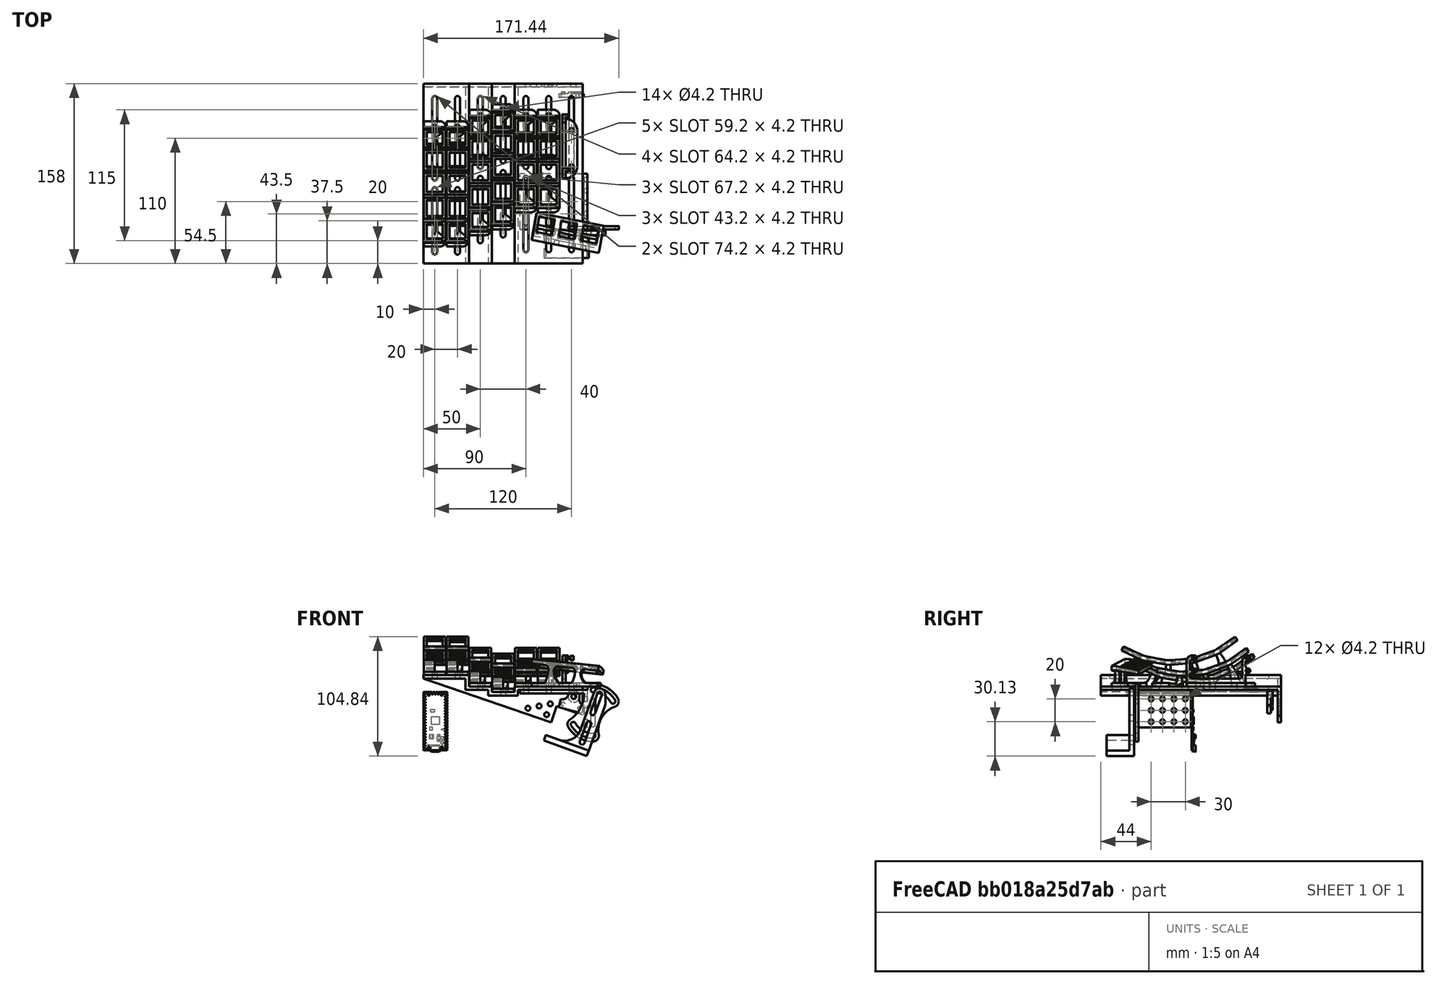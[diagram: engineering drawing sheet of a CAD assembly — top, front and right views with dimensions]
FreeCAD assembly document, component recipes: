
FREECAD ASSEMBLY — COMPONENT RECIPES ("Dactyl Chimera V3")

This assembly document has 15 components, labeled P0..P14 below (a component is one placed body or linked part). 14 of them carry a construction recipe — the FreeCAD feature program that regenerates the part from scratch, quoted from this document or its linked companion documents; the rest are supplied as boundary geometry only. No exploded tour is included for this assembly.
NOTE — document 2 of 4 of this assembly tour. The two overview renders and the header above are repeated from document 1; the component sections below continue where the previous document stopped.
COMPONENT P2 — recipe-attached ("RingArch", modeled in this document).
Construction recipe (the document's own serialized feature program — sketch geometry with constraints, then the solid features built on it; lengths are millimeters unless a unit is written):

FEATURE [Sketcher::SketchObject] Sketch012
  FullyConstrained = true
  MapMode = 5
  Placement = pos=(0,0,0) rot=(0.57735,0.57735,0.57735;2.0944rad)
  Support = -> [YZ_Plane002]
  expr: Constraints[147] = <<Spreadsheet>>.ModRowKey
  expr: Constraints[148] = <<Spreadsheet>>.ZRowKey
  expr: Constraints[149] = <<Spreadsheet>>.ARowKey
  expr: Constraints[150] = <<Spreadsheet>>.QRowKey
  expr: Constraints[151] = <<Spreadsheet>>.TopRowKey
  expr: Constraints[161] = <<Spreadsheet>>.Wiring
  sketch-geometry (61):
    g0: LineSegment StartX=-50.2141 StartY=25.1636 StartZ=0 EndX=-41.6042 EndY=21.1487 EndZ=0
    g1: LineSegment StartX=-41.6042 StartY=21.1487 StartZ=0 EndX=-32.9942 EndY=17.1338 EndZ=0
    g2: LineSegment StartX=-32.9942 StartY=17.1338 StartZ=0 EndX=-30.6407 EndY=16.3917 EndZ=0
    g3: LineSegment StartX=-30.6407 StartY=16.3917 StartZ=0 EndX=-21.285 EndY=14.7421 EndZ=0
    g4: LineSegment StartX=-21.285 StartY=14.7421 StartZ=0 EndX=-11.9293 EndY=13.0924 EndZ=0
    g5: LineSegment StartX=-11.9293 StartY=13.0924 StartZ=0 EndX=-9.46385 EndY=12.9848 EndZ=0
    g6: LineSegment StartX=-9.46385 StartY=12.9848 StartZ=0 EndX=0 EndY=13.8128 EndZ=0
    g7: LineSegment StartX=0 StartY=13.8128 StartZ=0 EndX=9.46385 EndY=14.6407 EndZ=0
    g8: LineSegment StartX=9.46385 StartY=14.6407 StartZ=0 EndX=11.8732 EndY=15.1749 EndZ=0
    g9: LineSegment StartX=11.8732 StartY=15.1749 StartZ=0 EndX=20.8002 EndY=18.4241 EndZ=0
    g10: LineSegment StartX=20.8002 StartY=18.4241 StartZ=0 EndX=29.7273 EndY=21.6733 EndZ=0
    g11: LineSegment StartX=29.7273 StartY=21.6733 StartZ=0 EndX=31.9163 EndY=22.8128 EndZ=0
    g12: LineSegment StartX=31.9163 StartY=22.8128 StartZ=0 EndX=39.6982 EndY=28.2617 EndZ=0
    g13: LineSegment StartX=39.6982 StartY=28.2617 StartZ=0 EndX=47.4802 EndY=33.7107 EndZ=0
    g14: LineSegment StartX=47.4802 StartY=33.7107 StartZ=0 EndX=49.7745 EndY=30.4341 EndZ=0
    g15: LineSegment StartX=49.7745 StartY=30.4341 StartZ=0 EndX=34.2106 EndY=19.5362 EndZ=0
    g16: LineSegment StartX=34.2106 StartY=19.5362 StartZ=0 EndX=31.0954 EndY=17.9145 EndZ=0
    g17: LineSegment StartX=31.0954 StartY=17.9145 StartZ=0 EndX=13.2412 EndY=11.4161 EndZ=0
    g18: LineSegment StartX=13.2412 StartY=11.4161 StartZ=0 EndX=9.81247 EndY=10.656 EndZ=0
    g19: LineSegment StartX=9.81247 StartY=10.656 StartZ=0 EndX=-9.11523 EndY=9 EndZ=0
    g20: LineSegment StartX=-9.11523 StartY=9 StartZ=0 EndX=-12.6239 EndY=9.15319 EndZ=0
    g21: LineSegment StartX=-12.6239 StartY=9.15319 StartZ=0 EndX=-31.3353 EndY=12.4525 EndZ=0
    g22: LineSegment StartX=-31.3353 StartY=12.4525 StartZ=0 EndX=-34.6847 EndY=13.5086 EndZ=0
    g23: LineSegment StartX=-34.6847 StartY=13.5086 StartZ=0 EndX=-51.9046 EndY=21.5383 EndZ=0
    g24: LineSegment StartX=-51.9046 StartY=21.5383 StartZ=0 EndX=-50.2141 EndY=25.1636 EndZ=0
    g25: LineSegment StartX=-34.6847 StartY=13.5086 StartZ=0 EndX=-32.9942 EndY=17.1338 EndZ=0
    g26: LineSegment StartX=-30.6407 StartY=16.3917 StartZ=0 EndX=-31.3353 EndY=12.4525 EndZ=0
    g27: LineSegment StartX=-11.9293 StartY=13.0924 StartZ=0 EndX=-12.6239 EndY=9.15319 EndZ=0
    g28: LineSegment StartX=-9.11523 StartY=9 StartZ=0 EndX=-9.46385 EndY=12.9848 EndZ=0
    g29: LineSegment StartX=9.46385 StartY=14.6407 StartZ=0 EndX=9.81247 EndY=10.656 EndZ=0
    g30: LineSegment StartX=13.2412 StartY=11.4161 StartZ=0 EndX=11.8732 EndY=15.1749 EndZ=0
    g31: LineSegment StartX=29.7273 StartY=21.6733 StartZ=0 EndX=31.0954 EndY=17.9145 EndZ=0
    g32: LineSegment StartX=34.2106 StartY=19.5362 StartZ=0 EndX=31.9163 EndY=22.8128 EndZ=0
    g33: LineSegment StartX=-41.6042 StartY=21.1487 StartZ=0 EndX=-39.4911 EndY=25.6802 EndZ=0
    g34: LineSegment StartX=-39.4911 StartY=25.6802 StartZ=0 EndX=-36.7722 EndY=24.4124 EndZ=0
    g35: LineSegment StartX=-36.7722 StartY=24.4124 StartZ=0 EndX=-32.546 EndY=33.4755 EndZ=0
    g36: LineSegment StartX=-21.6347 StartY=30.0351 StartZ=0 EndX=-23.3712 EndY=20.1871 EndZ=0
    g37: LineSegment StartX=-23.3712 StartY=20.1871 StartZ=0 EndX=-20.4167 EndY=19.6661 EndZ=0
    g38: LineSegment StartX=-20.4167 StartY=19.6661 StartZ=0 EndX=-17.4623 EndY=19.1452 EndZ=0
    g39: LineSegment StartX=-17.4623 StartY=19.1452 StartZ=0 EndX=-15.7258 EndY=28.9933 EndZ=0
    g40: LineSegment StartX=-4.29592 StartY=28.4942 StartZ=0 EndX=-3.42436 EndY=18.5323 EndZ=0
    g41: LineSegment StartX=-3.42436 StartY=18.5323 StartZ=0 EndX=-0.435779 EndY=18.7937 EndZ=0
    g42: LineSegment StartX=-0.435779 StartY=18.7937 StartZ=0 EndX=2.55281 EndY=19.0552 EndZ=0
    g43: LineSegment StartX=2.55281 StartY=19.0552 StartZ=0 EndX=1.68125 EndY=29.0171 EndZ=0
    g44: LineSegment StartX=12.8509 StartY=31.4934 StartZ=0 EndX=16.2711 EndY=22.0965 EndZ=0
    g45: LineSegment StartX=16.2711 StartY=22.0965 StartZ=0 EndX=19.0901 EndY=23.1225 EndZ=0
    g46: LineSegment StartX=19.0901 StartY=23.1225 StartZ=0 EndX=21.9092 EndY=24.1486 EndZ=0
    g47: LineSegment StartX=21.9092 StartY=24.1486 StartZ=0 EndX=18.489 EndY=33.5455 EndZ=0
    g48: LineSegment StartX=28.6371 StartY=38.8283 StartZ=0 EndX=34.3729 EndY=30.6368 EndZ=0
    g49: LineSegment StartX=34.3729 StartY=30.6368 StartZ=0 EndX=36.8304 EndY=32.3575 EndZ=0
    g50: ArcOfCircle CenterX=3.49974 CenterY=74.7282 CenterZ=0 NormalX=0 NormalY=0 NormalZ=1 AngleXU=0 Radius=43.8257 StartAngle=5.06145 EndAngle=5.32325
    g51: ArcOfCircle CenterX=-2.13841 CenterY=72.6761 CenterZ=0 NormalX=0 NormalY=0 NormalZ=1 AngleXU=0 Radius=43.8257 StartAngle=4.79966 EndAngle=5.06145
    g52: ArcOfCircle CenterX=-8.11558 CenterY=72.1532 CenterZ=0 NormalX=0 NormalY=0 NormalZ=1 AngleXU=0 Radius=43.8257 StartAngle=4.53786 EndAngle=4.79966
    g53: ArcOfCircle CenterX=-14.0244 CenterY=73.195 CenterZ=0 NormalX=0 NormalY=0 NormalZ=1 AngleXU=0 Radius=43.8257 StartAngle=4.27606 EndAngle=4.53786
    g54: LineSegment StartX=-20.4167 StartY=19.6661 StartZ=0 EndX=-21.285 EndY=14.7421 EndZ=0
    g55: LineSegment StartX=0 StartY=13.8128 StartZ=0 EndX=-0.435779 EndY=18.7937 EndZ=0
    g56: LineSegment StartX=19.0901 StartY=23.1225 StartZ=0 EndX=20.8002 EndY=18.4241 EndZ=0
    g57: LineSegment StartX=36.8304 StartY=32.3575 StartZ=0 EndX=39.6982 EndY=28.2617 EndZ=0
    g58: LineSegment StartX=-50 StartY=9 StartZ=0 EndX=-50 EndY=3 EndZ=0
    g59: LineSegment StartX=-50 StartY=9 StartZ=0 EndX=50 EndY=9 EndZ=0
    g60: LineSegment StartX=-70 StartY=9 StartZ=0 EndX=-50 EndY=9 EndZ=0
  constraints (176):
    c: Coincident(g0,g1)
    c: Coincident(g1,g2)
    c: Coincident(g2,g3)
    c: Coincident(g3,g4)
    c: Coincident(g4,g5)
    c: Coincident(g5,g6)
    c: Coincident(g6,g7)
    c: Coincident(g7,g8)
    c: Coincident(g8,g9)
    c: Coincident(g9,g10)
    c: Coincident(g10,g11)
    c: Coincident(g11,g12)
    c: Coincident(g12,g13)
    c: Coincident(g13,g14)
    c: Coincident(g14,g15)
    c: Coincident(g15,g16)
    c: Coincident(g16,g17)
    c: Coincident(g17,g18)
    c: Coincident(g18,g19)
    c: Coincident(g19,g20)
    c: Coincident(g20,g21)
    c: Coincident(g21,g22)
    c: Coincident(g22,g23)
    c: Coincident(g23,g24)
    c: Coincident(g24,g0)
    c: Coincident(g25,g22)
    c: Coincident(g25,g1)
    c: Coincident(g26,g2)
    c: Coincident(g26,g21)
    c: Coincident(g27,g4)
    c: Coincident(g27,g20)
    c: Coincident(g28,g19)
    c: Coincident(g28,g5)
    c: Coincident(g29,g7)
    c: Coincident(g29,g18)
    c: Coincident(g30,g17)
    c: Coincident(g30,g8)
    c: Coincident(g31,g10)
    c: Coincident(g31,g16)
    c: Coincident(g32,g15)
    c: Coincident(g32,g11)
    c: Equal(g32,g31)
    c: Equal(g30,g29)
    c: Equal(g28,g27)
    c: Equal(g26,g25)
    c: Perpendicular(g24,g23)
    c: Perpendicular(g23,g25)
    c: Perpendicular(g21,g26)
    c: Perpendicular(g27,g21)
    c: Perpendicular(g19,g28)
    c: Perpendicular(g29,g19)
    c: Perpendicular(g17,g30)
    c: Perpendicular(g31,g17)
    c: Perpendicular(g15,g32)
    c: Perpendicular(g14,g15)
    c: Perpendicular(g24,g0)
    c: Perpendicular(g26,g3)
    c: Perpendicular(g28,g6)
    c: Perpendicular(g30,g9)
    c: Perpendicular(g32,g12)
    c: Parallel(g13,g12)
    c: Parallel(g10,g9)
    c: Parallel(g7,g6)
    c: Parallel(g4,g3)
    c: Parallel(g1,g0)
    c: Coincident(g0,g33)
    c: Coincident(g33,g34)
    c: Coincident(g34,g35)
    c: Coincident(g36,g37)
    c: Coincident(g37,g38)
    c: Coincident(g38,g39)
    c: Coincident(g40,g41)
    c: Coincident(g41,g42)
    c: Coincident(g42,g43)
    c: Coincident(g44,g45)
    c: Coincident(g45,g46)
    c: Coincident(g46,g47)
    c: Coincident(g48,g49)
    c: Coincident(g50,g47)
    c: Coincident(g50,g48)
    c: Coincident(g51,g43)
    c: Coincident(g51,g44)
    c: Coincident(g52,g39)
    c: Coincident(g52,g40)
    c: Coincident(g53,g35)
    c: Coincident(g53,g36)
    c: Coincident(g54,g37)
    c: Coincident(g54,g3)
    c: Coincident(g55,g6)
    c: Coincident(g55,g41)
    c: Coincident(g56,g45)
    c: Coincident(g56,g9)
    c: Coincident(g57,g49)
    c: Coincident(g57,g12)
    c: Equal(g34,g37)
    c: Equal(g37,g38)
    c: Equal(g38,g41)
    c: Equal(g41,g42)
    c: Equal(g42,g45)
    c: Equal(g45,g46)
    c: Equal(g46,g49)
    c: Perpendicular(g1,g33)
    c: Perpendicular(g4,g54)
    c: Perpendicular(g7,g55)
    c: Perpendicular(g10,g56)
    c: Perpendicular(g13,g57)
    c: Perpendicular(g49,g57)
    c: Perpendicular(g46,g56)
    c: Perpendicular(g56,g45)
    c: Perpendicular(g55,g42)
    c: Perpendicular(g41,g55)
    c: Perpendicular(g54,g38)
    c: Perpendicular(g37,g54)
    c: Perpendicular(g33,g34)
    c: Perpendicular(g35,g34)
    c: Perpendicular(g53,g35)
    c: Perpendicular(g53,g36)
    c: Perpendicular(g37,g36)
    c: Perpendicular(g39,g38)
    c: Perpendicular(g52,g39)
    c: Perpendicular(g52,g40)
    c: Perpendicular(g41,g40)
    c: Perpendicular(g43,g42)
    c: Perpendicular(g51,g43)
    c: Perpendicular(g51,g44)
    c: Perpendicular(g45,g44)
    c: Perpendicular(g47,g46)
    c: Perpendicular(g50,g47)
    c: Perpendicular(g50,g48)
    c: Perpendicular(g49,g48)
    c: Distance(g33,g37) = 20
    c: Distance(g41,g37) = 20
    c: Distance(g41,g45) = 20
    c: Distance(g49,g45) = 20
    c: Equal(g13,g12)
    c: Equal(g10,g9)
    c: Equal(g7,g6)
    c: Equal(g4,g3)
    c: Equal(g1,g0)
    c: Distance(g35) = 10
    c: Distance(g36) = 10
    c: Distance(g39) = 10
    c: Distance(g40) = 10
    c: Distance(g43) = 10
    c: Distance(g44) = 10
    c: Distance(g47) = 10
    c: Distance(g48) = 10
    c: Distance(g33) = 5
    c: Distance(g54) = 5
    c: Distance(g55) = 5
    c: Distance(g56) = 5
    c: Distance(g57) = 5
    c: Distance(g19) = 19
    c: Distance(g28) = 4
    c: Equal(g23,g21)
    c: Equal(g21,g19)
    c: Equal(g19,g17)
    c: Equal(g17,g15)
    c: Vertical(g58)
    c: Coincident(g59,g58)
    c: Horizontal(g59)
    c: DistanceY(g58,g58) = 6
    c: DistanceX(g59,g59) = 100
    c: DistanceX(g58,g-1) = 50
    c: DistanceY(g-1,g58) = 3
    c: Distance(g42) = 3
    c: Horizontal(g60)
    c: Angle(g60,g55) = 1.65806
    c: Coincident(g60,g58)
    c: DistanceX(g60,g60) = 20
    c: Angle(g56,g57) = 0.261799
    c: Angle(g55,g56) = 0.261799
    c: Angle(g54,g55) = 0.261799
    c: Angle(g33,g54) = 0.261799
    c: PointOnObject(g6,g-2)
    c: PointOnObject(g19,g59)
FEATURE [PartDesign::Pad] Pad008  label="RArch"
  Direction = (1,-2e-16,3e-16)
  Length = 19
  Length2 = 100
  Midplane = true
  Placement = pos=(0,0,0) rot=(0.57735,0.57735,0.57735;2.0944rad)
  Profile = -> Sketch012
  ReferenceAxis = -> Sketch012 [N_Axis]
  Type = 0
FEATURE [Sketcher::SketchObject] Sketch013
  ExternalGeometry = -> [Sketch012]
  FullyConstrained = true
  MapMode = 5
  Placement = pos=(0,0,0) rot=(0.57735,0.57735,0.57735;2.0944rad)
  Support = -> [YZ_Plane002]
  sketch-geometry (75):
    g0: LineSegment StartX=-49.1265 StartY=24.6564 StartZ=0 EndX=-50.817 EndY=21.0312 EndZ=0
    g1: LineSegment StartX=-49.6388 StartY=20.4818 StartZ=0 EndX=-47.9483 EndY=24.107 EndZ=0
    g2: LineSegment StartX=-35.26 StartY=18.1904 StartZ=0 EndX=-36.9505 EndY=14.5651 EndZ=0
    g3: LineSegment StartX=-35.7723 StartY=14.0157 StartZ=0 EndX=-34.0818 EndY=17.641 EndZ=0
    g4: LineSegment StartX=-41.6042 StartY=21.1487 StartZ=0 EndX=-43.2946 EndY=17.5235 EndZ=0
    g5: LineSegment StartX=-29.4589 StartY=16.1834 StartZ=0 EndX=-30.1535 EndY=12.2441 EndZ=0
    g6: LineSegment StartX=-28.8732 StartY=12.0184 StartZ=0 EndX=-28.1786 EndY=15.9576 EndZ=0
    g7: LineSegment StartX=-21.285 StartY=14.7421 StartZ=0 EndX=-21.9796 EndY=10.8028 EndZ=0
    g8: LineSegment StartX=-15.0859 StartY=9.58731 StartZ=0 EndX=-14.3913 EndY=13.5265 EndZ=0
    g9: LineSegment StartX=-13.1111 StartY=13.3008 StartZ=0 EndX=-13.8057 EndY=9.36157 EndZ=0
    g10: LineSegment StartX=-8.26842 StartY=13.0894 StartZ=0 EndX=-7.91979 EndY=9.10459 EndZ=0
    g11: LineSegment StartX=-6.62474 StartY=9.21789 StartZ=0 EndX=-6.97336 EndY=13.2027 EndZ=0
    g12: LineSegment StartX=0 StartY=13.8128 StartZ=0 EndX=0.348623 EndY=9.82798 EndZ=0
    g13: LineSegment StartX=7.32199 StartY=10.4381 StartZ=0 EndX=6.97336 EndY=14.4228 EndZ=0
    g14: LineSegment StartX=8.26842 StartY=14.5362 StartZ=0 EndX=8.61704 EndY=10.5514 EndZ=0
    g15: LineSegment StartX=14.3689 StartY=11.8265 StartZ=0 EndX=13.0008 EndY=15.5853 EndZ=0
    g16: LineSegment StartX=14.2224 StartY=16.0299 StartZ=0 EndX=15.5905 EndY=12.2711 EndZ=0
    g17: LineSegment StartX=22.1683 StartY=14.6653 StartZ=0 EndX=20.8002 EndY=18.4241 EndZ=0
    g18: LineSegment StartX=27.3781 StartY=20.8182 StartZ=0 EndX=28.7462 EndY=17.0594 EndZ=0
    g19: LineSegment StartX=29.9678 StartY=17.5041 StartZ=0 EndX=28.5997 EndY=21.2628 EndZ=0
    g20: LineSegment StartX=32.8993 StartY=23.5011 StartZ=0 EndX=35.1936 EndY=20.2244 EndZ=0
    g21: LineSegment StartX=36.2585 StartY=20.9701 StartZ=0 EndX=33.9642 EndY=24.2467 EndZ=0
    g22: LineSegment StartX=39.6982 StartY=28.2617 StartZ=0 EndX=41.9925 EndY=24.9851 EndZ=0
    g23: LineSegment StartX=47.7266 StartY=29.0002 StartZ=0 EndX=45.4323 EndY=32.2768 EndZ=0
    g24: LineSegment StartX=46.4972 StartY=33.0224 StartZ=0 EndX=48.7915 EndY=29.7458 EndZ=0
    g25: LineSegment StartX=45.4323 StartY=32.2768 StartZ=0 EndX=39.6982 EndY=28.2617 EndZ=0
    g26: LineSegment StartX=39.6982 StartY=28.2617 StartZ=0 EndX=33.9642 EndY=24.2467 EndZ=0
    g27: LineSegment StartX=33.9642 StartY=24.2467 StartZ=0 EndX=34.7672 EndY=23.0999 EndZ=0
    g28: LineSegment StartX=34.7672 StartY=23.0999 StartZ=0 EndX=33.7023 EndY=22.3542 EndZ=0
    g29: LineSegment StartX=33.7023 StartY=22.3542 StartZ=0 EndX=35.1936 EndY=20.2244 EndZ=0
    g30: LineSegment StartX=35.1936 StartY=20.2244 StartZ=0 EndX=41.9925 EndY=24.9851 EndZ=0
    g31: LineSegment StartX=41.9925 StartY=24.9851 StartZ=0 EndX=48.7915 EndY=29.7458 EndZ=0
    g32: LineSegment StartX=48.7915 StartY=29.7458 StartZ=0 EndX=47.3002 EndY=31.8756 EndZ=0
    g33: LineSegment StartX=47.3002 StartY=31.8756 StartZ=0 EndX=46.2353 EndY=31.13 EndZ=0
    g34: LineSegment StartX=46.2353 StartY=31.13 StartZ=0 EndX=45.4323 EndY=32.2768 EndZ=0
    g35: LineSegment StartX=27.3781 StartY=20.8182 StartZ=0 EndX=20.8002 EndY=18.4241 EndZ=0
    g36: LineSegment StartX=20.8002 StartY=18.4241 StartZ=0 EndX=14.2224 EndY=16.0299 EndZ=0
    g37: LineSegment StartX=14.2224 StartY=16.0299 StartZ=0 EndX=14.7012 EndY=14.7144 EndZ=0
    g38: LineSegment StartX=14.7012 StartY=14.7144 StartZ=0 EndX=13.4796 EndY=14.2697 EndZ=0
    g39: LineSegment StartX=13.4796 StartY=14.2697 StartZ=0 EndX=14.3689 EndY=11.8265 EndZ=0
    g40: LineSegment StartX=14.3689 StartY=11.8265 StartZ=0 EndX=22.1683 EndY=14.6653 EndZ=0
    g41: LineSegment StartX=22.1683 StartY=14.6653 StartZ=0 EndX=29.9678 EndY=17.5041 EndZ=0
    g42: LineSegment StartX=29.9678 StartY=17.5041 StartZ=0 EndX=29.0785 EndY=19.9473 EndZ=0
    g43: LineSegment StartX=29.0785 StartY=19.9473 StartZ=0 EndX=27.8569 EndY=19.5026 EndZ=0
    g44: LineSegment StartX=27.8569 StartY=19.5026 StartZ=0 EndX=27.3781 EndY=20.8182 EndZ=0
    g45: LineSegment StartX=-6.97336 StartY=13.2027 StartZ=0 EndX=-6.85134 EndY=11.808 EndZ=0
    g46: LineSegment StartX=-6.85134 StartY=11.808 StartZ=0 EndX=-8.14639 EndY=11.6947 EndZ=0
    g47: LineSegment StartX=-8.14639 StartY=11.6947 StartZ=0 EndX=-7.91979 EndY=9.10459 EndZ=0
    g48: LineSegment StartX=8.61704 StartY=10.5514 StartZ=0 EndX=8.39044 EndY=13.1415 EndZ=0
    g49: LineSegment StartX=8.39044 StartY=13.1415 StartZ=0 EndX=7.09538 EndY=13.0282 EndZ=0
    g50: LineSegment StartX=7.09538 StartY=13.0282 StartZ=0 EndX=6.97336 EndY=14.4228 EndZ=0
    g51: LineSegment StartX=6.97336 StartY=14.4228 StartZ=0 EndX=0 EndY=13.8128 EndZ=0
    g52: LineSegment StartX=0 StartY=13.8128 StartZ=0 EndX=-6.97336 EndY=13.2027 EndZ=0
    g53: LineSegment StartX=-7.91979 StartY=9.10459 StartZ=0 EndX=0.348623 EndY=9.82798 EndZ=0
    g54: LineSegment StartX=0.348623 StartY=9.82798 StartZ=0 EndX=8.61704 EndY=10.5514 EndZ=0
    g55: LineSegment StartX=-21.285 StartY=14.7421 StartZ=0 EndX=-28.1786 EndY=15.9576 EndZ=0
    g56: LineSegment StartX=-28.1786 StartY=15.9576 StartZ=0 EndX=-28.4218 EndY=14.5789 EndZ=0
    g57: LineSegment StartX=-28.4218 StartY=14.5789 StartZ=0 EndX=-29.702 EndY=14.8046 EndZ=0
    g58: LineSegment StartX=-29.702 StartY=14.8046 StartZ=0 EndX=-30.1535 EndY=12.2441 EndZ=0
    g59: LineSegment StartX=-30.1535 StartY=12.2441 StartZ=0 EndX=-21.9796 EndY=10.8028 EndZ=0
    g60: LineSegment StartX=-21.9796 StartY=10.8028 StartZ=0 EndX=-13.8057 EndY=9.36157 EndZ=0
    g61: LineSegment StartX=-13.8057 StartY=9.36157 StartZ=0 EndX=-13.3542 EndY=11.9221 EndZ=0
    g62: LineSegment StartX=-13.3542 StartY=11.9221 StartZ=0 EndX=-14.6345 EndY=12.1478 EndZ=0
    g63: LineSegment StartX=-14.6345 StartY=12.1478 StartZ=0 EndX=-14.3913 EndY=13.5265 EndZ=0
    g64: LineSegment StartX=-14.3913 StartY=13.5265 StartZ=0 EndX=-21.285 EndY=14.7421 EndZ=0
    g65: LineSegment StartX=-41.6042 StartY=21.1487 StartZ=0 EndX=-47.9483 EndY=24.107 EndZ=0
    g66: LineSegment StartX=-47.9483 StartY=24.107 StartZ=0 EndX=-48.54 EndY=22.8382 EndZ=0
    g67: LineSegment StartX=-48.54 StartY=22.8382 StartZ=0 EndX=-49.7182 EndY=23.3876 EndZ=0
    g68: LineSegment StartX=-49.7182 StartY=23.3876 StartZ=0 EndX=-50.817 EndY=21.0312 EndZ=0
    g69: LineSegment StartX=-50.817 StartY=21.0312 StartZ=0 EndX=-43.2946 EndY=17.5235 EndZ=0
    g70: LineSegment StartX=-43.2946 StartY=17.5235 StartZ=0 EndX=-35.7723 EndY=14.0157 EndZ=0
    g71: LineSegment StartX=-35.7723 StartY=14.0157 StartZ=0 EndX=-34.6735 EndY=16.3721 EndZ=0
    g72: LineSegment StartX=-34.6735 StartY=16.3721 StartZ=0 EndX=-35.8517 EndY=16.9215 EndZ=0
    g73: LineSegment StartX=-35.8517 StartY=16.9215 StartZ=0 EndX=-35.26 EndY=18.1904 EndZ=0
    g74: LineSegment StartX=-35.26 StartY=18.1904 StartZ=0 EndX=-41.6042 EndY=21.1487 EndZ=0
  constraints (215):
    c: PointOnObject(g0,g-16)
    c: PointOnObject(g0,g-17)
    c: PointOnObject(g1,g-17)
    c: PointOnObject(g1,g-16)
    c: PointOnObject(g2,g-15)
    c: PointOnObject(g2,g-17)
    c: PointOnObject(g3,g-17)
    c: PointOnObject(g3,g-15)
    c: Coincident(g4,g-16)
    c: PointOnObject(g4,g-17)
    c: PointOnObject(g5,g-14)
    c: PointOnObject(g5,g-12)
    c: PointOnObject(g6,g-12)
    c: PointOnObject(g6,g-14)
    c: Coincident(g7,g-14)
    c: PointOnObject(g7,g-12)
    c: PointOnObject(g8,g-12)
    c: PointOnObject(g8,g-13)
    c: PointOnObject(g9,g-13)
    c: PointOnObject(g9,g-12)
    c: PointOnObject(g10,g-10)
    c: PointOnObject(g10,g-11)
    c: PointOnObject(g11,g-11)
    c: PointOnObject(g11,g-10)
    c: Coincident(g12,g-10)
    c: PointOnObject(g12,g-11)
    c: PointOnObject(g13,g-9)
    c: PointOnObject(g14,g-9)
    c: PointOnObject(g14,g-11)
    c: PointOnObject(g15,g-6)
    c: PointOnObject(g15,g-8)
    c: PointOnObject(g16,g-8)
    c: PointOnObject(g16,g-6)
    c: PointOnObject(g17,g-6)
    c: Coincident(g17,g-8)
    c: PointOnObject(g18,g-7)
    c: PointOnObject(g18,g-6)
    c: PointOnObject(g19,g-6)
    c: PointOnObject(g19,g-7)
    c: PointOnObject(g20,g-4)
    c: PointOnObject(g20,g-5)
    c: PointOnObject(g21,g-5)
    c: PointOnObject(g21,g-4)
    c: Coincident(g22,g-4)
    c: PointOnObject(g22,g-5)
    c: PointOnObject(g23,g-5)
    c: PointOnObject(g23,g-3)
    c: PointOnObject(g24,g-3)
    c: PointOnObject(g24,g-5)
    c: Perpendicular(g-3,g24)
    c: Perpendicular(g23,g-3)
    c: Perpendicular(g22,g-5)
    c: Perpendicular(g21,g-4)
    c: Perpendicular(g20,g-4)
    c: Perpendicular(g-7,g19)
    c: Perpendicular(g-6,g17)
    c: Perpendicular(g-8,g16)
    c: Perpendicular(g15,g-8)
    c: Perpendicular(g-9,g14)
    c: Perpendicular(g13,g-9)
    c: Perpendicular(g12,g-11)
    c: Perpendicular(g-10,g11)
    c: Perpendicular(g-10,g10)
    c: Perpendicular(g-13,g9)
    c: Perpendicular(g-13,g8)
    c: Perpendicular(g-12,g7)
    c: Perpendicular(g-14,g6)
    c: Perpendicular(g-14,g5)
    c: Perpendicular(g-15,g3)
    c: Perpendicular(g2,g-15)
    c: Perpendicular(g-17,g4)
    c: Perpendicular(g-16,g1)
    c: Perpendicular(g-16,g0)
    c: Distance(g2,g1) = 14
    c: Distance(g3,g0) = 16.6
    c: Distance(g6,g8) = 14
    c: Distance(g9,g5) = 16.6
    c: Distance(g13,g11) = 14
    c: Distance(g14,g10) = 16.6
    c: Distance(g15,g19) = 16.6
    c: Distance(g16,g18) = 14
    c: Perpendicular(g-7,g18)
    c: Distance(g24,g20) = 16.6
    c: Distance(g23,g21) = 14
    c: Coincident(g23,g25)
    c: Coincident(g25,g22)
    c: Coincident(g25,g26)
    c: Coincident(g26,g21)
    c: Coincident(g26,g27)
    c: Coincident(g27,g28)
    c: Coincident(g28,g29)
    c: Coincident(g29,g20)
    c: Coincident(g29,g30)
    c: Coincident(g30,g22)
    c: Coincident(g30,g31)
    c: Coincident(g31,g24)
    c: Coincident(g31,g32)
    c: Coincident(g32,g33)
    c: Coincident(g33,g34)
    c: Coincident(g34,g25)
    c: Equal(g25,g26)
    c: Equal(g31,g30)
    c: Distance(g26,g27) = 1.4
    c: Distance(g27,g21) = 2.6
    c: Distance(g29,g28) = 2.6
    c: Distance(g28,g20) = 1.4
    c: Distance(g33,g25) = 1.4
    c: Distance(g32,g24) = 1.4
    c: Distance(g32,g31) = 2.6
    c: Distance(g33,g23) = 2.6
    c: Coincident(g18,g35)
    c: Coincident(g35,g17)
    c: Coincident(g35,g36)
    c: Coincident(g36,g16)
    c: Coincident(g36,g37)
    c: Coincident(g37,g38)
    c: Coincident(g38,g39)
    c: Coincident(g39,g15)
    c: Coincident(g39,g40)
    c: Coincident(g40,g17)
    c: Coincident(g40,g41)
    c: Coincident(g41,g19)
    c: Coincident(g41,g42)
    c: Coincident(g42,g43)
    c: Coincident(g43,g44)
    c: Coincident(g44,g35)
    c: Coincident(g45,g46)
    c: Coincident(g46,g47)
    c: Coincident(g47,g10)
    c: Coincident(g48,g49)
    c: Coincident(g49,g50)
    c: Coincident(g50,g51)
    c: Coincident(g51,g12)
    c: Coincident(g51,g52)
    c: Coincident(g52,g45)
    c: Equal(g52,g51)
    c: Coincident(g45,g11)
    c: Coincident(g50,g13)
    c: Distance(g50,g49) = 1.4
    c: Distance(g13,g49) = 2.6
    c: Distance(g14,g48) = 1.4
    c: Distance(g48,g14) = 2.6
    c: Coincident(g47,g53)
    c: Coincident(g53,g12)
    c: Coincident(g53,g54)
    c: Coincident(g54,g48)
    c: Coincident(g48,g14)
    c: Equal(g54,g53)
    c: PointOnObject(g13,g-11)
    c: Distance(g45,g45) = 1.4
    c: Distance(g45,g11) = 2.6
    c: Distance(g10,g46) = 1.4
    c: Distance(g46,g47) = 2.6
    c: Coincident(g7,g55)
    c: Coincident(g55,g56)
    c: Coincident(g56,g57)
    c: Coincident(g57,g58)
    c: Coincident(g58,g5)
    c: Coincident(g58,g59)
    c: Coincident(g59,g60)
    c: Coincident(g60,g9)
    c: Coincident(g60,g61)
    c: Coincident(g61,g62)
    c: Coincident(g62,g63)
    c: Coincident(g63,g8)
    c: Coincident(g63,g64)
    c: Coincident(g64,g55)
    c: Coincident(g55,g6)
    c: Equal(g55,g64)
    c: Coincident(g59,g7)
    c: Equal(g59,g60)
    c: Distance(g61,g60) = 2.6
    c: Distance(g62,g8) = 2.6
    c: Distance(g57,g5) = 1.4
    c: Distance(g55,g56) = 1.4
    c: Distance(g6,g56) = 2.6
    c: Distance(g57,g58) = 2.6
    c: Distance(g62,g63) = 1.4
    c: Distance(g61,g9) = 1.4
    c: Coincident(g4,g65)
    c: Coincident(g65,g1)
    c: Coincident(g65,g66)
    c: Coincident(g66,g67)
    c: Coincident(g67,g68)
    c: Coincident(g68,g0)
    c: Coincident(g68,g69)
    c: Coincident(g69,g4)
    c: Coincident(g69,g70)
    c: Coincident(g70,g3)
    c: Coincident(g70,g71)
    c: Coincident(g71,g72)
    c: Coincident(g72,g73)
    c: Coincident(g73,g2)
    c: Coincident(g73,g74)
    c: Coincident(g74,g65)
    c: Equal(g74,g65)
    c: Equal(g70,g69)
    c: Distance(g73,g72) = 1.4
    c: Distance(g71,g3) = 1.4
    c: Distance(g72,g2) = 2.6
    c: Distance(g70,g71) = 2.6
    c: Distance(g66,g65) = 1.4
    c: Distance(g0,g67) = 1.4
    c: Distance(g67,g68) = 2.6
    c: Distance(g66,g1) = 2.6
    c: Equal(g36,g35)
    c: Equal(g41,g40)
    c: Distance(g41,g42) = 2.6
    c: Distance(g42,g19) = 1.4
    c: Distance(g43,g35) = 1.4
    c: Distance(g43,g18) = 2.6
    c: Distance(g37,g36) = 1.4
    c: Distance(g38,g15) = 1.4
    c: Distance(g38,g39) = 2.6
    c: Distance(g37,g16) = 2.6
FEATURE [PartDesign::Pocket] Pocket004  label="RMX sockets"
  BaseFeature = -> Pad008
  Direction = (-1,2e-16,-3e-16)
  Length = 14
  Length2 = 100
  Midplane = true
  Placement = pos=(0,0,0) rot=(0.57735,0.57735,0.57735;2.0944rad)
  Profile = -> Sketch013
  Type = 0
FEATURE [Sketcher::SketchObject] Sketch014
  ExternalGeometry = -> [Sketch013]
  FullyConstrained = true
  MapMode = 5
  Placement = pos=(0,0,0) rot=(0.57735,0.57735,0.57735;2.0944rad)
  Support = -> [YZ_Plane002]
  sketch-geometry (55):
    g0: LineSegment StartX=27.8569 StartY=19.5026 StartZ=0 EndX=27.7885 EndY=19.6906 EndZ=0
    g1: LineSegment StartX=27.7885 StartY=19.6906 StartZ=0 EndX=14.6328 EndY=14.9023 EndZ=0
    g2: LineSegment StartX=14.6328 StartY=14.9023 StartZ=0 EndX=14.7012 EndY=14.7144 EndZ=0
    g3: LineSegment StartX=14.7012 StartY=14.7144 StartZ=0 EndX=13.4796 EndY=14.2697 EndZ=0
    g4: LineSegment StartX=13.4796 StartY=14.2697 StartZ=0 EndX=13.7532 EndY=13.518 EndZ=0
    g5: LineSegment StartX=13.7532 StartY=13.518 StartZ=0 EndX=29.3521 EndY=19.1955 EndZ=0
    g6: LineSegment StartX=29.3521 StartY=19.1955 StartZ=0 EndX=29.0785 EndY=19.9473 EndZ=0
    g7: LineSegment StartX=29.0785 StartY=19.9473 StartZ=0 EndX=27.8569 EndY=19.5026 EndZ=0
    g8: LineSegment StartX=7.07795 StartY=13.2274 StartZ=0 EndX=7.09538 EndY=13.0282 EndZ=0
    g9: LineSegment StartX=7.09538 StartY=13.0282 StartZ=0 EndX=8.39044 EndY=13.1415 EndZ=0
    g10: LineSegment StartX=8.39044 StartY=13.1415 StartZ=0 EndX=8.46016 EndY=12.3445 EndZ=0
    g11: LineSegment StartX=8.46016 StartY=12.3445 StartZ=0 EndX=-8.07667 EndY=10.8977 EndZ=0
    g12: LineSegment StartX=-8.07667 StartY=10.8977 StartZ=0 EndX=-8.14639 EndY=11.6947 EndZ=0
    g13: LineSegment StartX=-8.14639 StartY=11.6947 StartZ=0 EndX=-6.85134 EndY=11.808 EndZ=0
    g14: LineSegment StartX=-6.85134 StartY=11.808 StartZ=0 EndX=-6.86877 EndY=12.0072 EndZ=0
    g15: LineSegment StartX=-6.86877 StartY=12.0072 StartZ=0 EndX=7.07795 EndY=13.2274 EndZ=0
    g16: LineSegment StartX=0 StartY=13.8128 StartZ=0 EndX=0.104587 EndY=12.6173 EndZ=0
    g17: LineSegment StartX=0.104587 StartY=12.6173 StartZ=0 EndX=0.191743 EndY=11.6211 EndZ=0
    g18: LineSegment StartX=0.191743 StartY=11.6211 StartZ=0 EndX=0.348623 EndY=9.82798 EndZ=0
    g19: LineSegment StartX=20.8002 StartY=18.4241 StartZ=0 EndX=21.2107 EndY=17.2964 EndZ=0
    g20: LineSegment StartX=21.2107 StartY=17.2964 StartZ=0 EndX=21.5527 EndY=16.3567 EndZ=0
    g21: LineSegment StartX=21.5527 StartY=16.3567 StartZ=0 EndX=22.1683 EndY=14.6653 EndZ=0
    g22: LineSegment StartX=39.6982 StartY=28.2617 StartZ=0 EndX=40.3865 EndY=27.2788 EndZ=0
    g23: LineSegment StartX=40.3865 StartY=27.2788 StartZ=0 EndX=40.9601 EndY=26.4596 EndZ=0
    g24: LineSegment StartX=40.9601 StartY=26.4596 StartZ=0 EndX=41.9925 EndY=24.9851 EndZ=0
    g25: LineSegment StartX=34.6525 StartY=23.2637 StartZ=0 EndX=46.1206 EndY=31.2938 EndZ=0
    g26: LineSegment StartX=46.1206 StartY=31.2938 StartZ=0 EndX=46.2353 EndY=31.13 EndZ=0
    g27: LineSegment StartX=46.2353 StartY=31.13 StartZ=0 EndX=47.3002 EndY=31.8756 EndZ=0
    g28: LineSegment StartX=47.3002 StartY=31.8756 StartZ=0 EndX=47.7591 EndY=31.2203 EndZ=0
    g29: LineSegment StartX=47.7591 StartY=31.2203 StartZ=0 EndX=34.1611 EndY=21.6989 EndZ=0
    g30: LineSegment StartX=34.1611 StartY=21.6989 StartZ=0 EndX=33.7023 EndY=22.3542 EndZ=0
    g31: LineSegment StartX=33.7023 StartY=22.3542 StartZ=0 EndX=34.7672 EndY=23.0999 EndZ=0
    g32: LineSegment StartX=34.7672 StartY=23.0999 StartZ=0 EndX=34.6525 EndY=23.2637 EndZ=0
    g33: LineSegment StartX=-48.54 StartY=22.8382 StartZ=0 EndX=-49.7182 EndY=23.3876 EndZ=0
    g34: LineSegment StartX=-49.7182 StartY=23.3876 StartZ=0 EndX=-50.0563 EndY=22.6626 EndZ=0
    g35: LineSegment StartX=-50.0563 StartY=22.6626 StartZ=0 EndX=-35.0116 EndY=15.6471 EndZ=0
    g36: LineSegment StartX=-35.0116 StartY=15.6471 StartZ=0 EndX=-34.6735 EndY=16.3721 EndZ=0
    g37: LineSegment StartX=-34.6735 StartY=16.3721 StartZ=0 EndX=-35.8517 EndY=16.9215 EndZ=0
    g38: LineSegment StartX=-35.8517 StartY=16.9215 StartZ=0 EndX=-35.7672 EndY=17.1028 EndZ=0
    g39: LineSegment StartX=-35.7672 StartY=17.1028 StartZ=0 EndX=-48.4555 EndY=23.0195 EndZ=0
    g40: LineSegment StartX=-48.4555 StartY=23.0195 StartZ=0 EndX=-48.54 EndY=22.8382 EndZ=0
    g41: LineSegment StartX=-41.6042 StartY=21.1487 StartZ=0 EndX=-42.1113 EndY=20.0611 EndZ=0
    g42: LineSegment StartX=-42.1113 StartY=20.0611 StartZ=0 EndX=-42.5339 EndY=19.1548 EndZ=0
    g43: LineSegment StartX=-42.5339 StartY=19.1548 StartZ=0 EndX=-43.2946 EndY=17.5235 EndZ=0
    g44: LineSegment StartX=-28.387 StartY=14.7758 StartZ=0 EndX=-28.4218 EndY=14.5789 EndZ=0
    g45: LineSegment StartX=-28.4218 StartY=14.5789 StartZ=0 EndX=-29.702 EndY=14.8046 EndZ=0
    g46: LineSegment StartX=-29.702 StartY=14.8046 StartZ=0 EndX=-29.8409 EndY=14.0168 EndZ=0
    g47: LineSegment StartX=-29.8409 StartY=14.0168 StartZ=0 EndX=-13.4931 EndY=11.1342 EndZ=0
    g48: LineSegment StartX=-13.4931 StartY=11.1342 StartZ=0 EndX=-13.3542 EndY=11.9221 EndZ=0
    g49: LineSegment StartX=-13.3542 StartY=11.9221 StartZ=0 EndX=-14.6345 EndY=12.1478 EndZ=0
    g50: LineSegment StartX=-14.6345 StartY=12.1478 StartZ=0 EndX=-14.5997 EndY=12.3448 EndZ=0
    g51: LineSegment StartX=-14.5997 StartY=12.3448 StartZ=0 EndX=-28.387 EndY=14.7758 EndZ=0
    g52: LineSegment StartX=-21.285 StartY=14.7421 StartZ=0 EndX=-21.4934 EndY=13.5603 EndZ=0
    g53: LineSegment StartX=-21.4934 StartY=13.5603 StartZ=0 EndX=-21.667 EndY=12.5755 EndZ=0
    g54: LineSegment StartX=-21.667 StartY=12.5755 StartZ=0 EndX=-21.9796 EndY=10.8028 EndZ=0
  constraints (140):
    c: Coincident(g-3,g0)
    c: Coincident(g0,g1)
    c: Coincident(g1,g2)
    c: Coincident(g2,g3)
    c: Coincident(g3,g4)
    c: Coincident(g4,g5)
    c: Coincident(g5,g6)
    c: Coincident(g6,g-4)
    c: Coincident(g6,g7)
    c: Coincident(g7,g0)
    c: Coincident(g3,g-6)
    c: Coincident(g2,g-5)
    c: Coincident(g8,g-7)
    c: Coincident(g8,g9)
    c: Coincident(g9,g-8)
    c: Coincident(g9,g10)
    c: Coincident(g10,g11)
    c: Coincident(g11,g12)
    c: Coincident(g12,g-9)
    c: Coincident(g12,g13)
    c: Coincident(g13,g-10)
    c: Coincident(g13,g14)
    c: Coincident(g14,g15)
    c: Coincident(g15,g8)
    c: PointOnObject(g10,g-8)
    c: PointOnObject(g1,g-5)
    c: PointOnObject(g0,g-3)
    c: PointOnObject(g5,g-4)
    c: PointOnObject(g4,g-6)
    c: PointOnObject(g8,g-7)
    c: PointOnObject(g11,g-9)
    c: PointOnObject(g14,g-10)
    c: Coincident(g16,g-11)
    c: PointOnObject(g16,g15)
    c: Coincident(g17,g16)
    c: PointOnObject(g17,g11)
    c: Coincident(g18,g-12)
    c: Angle(g16,g17) = 3.14159
    c: Angle(g17,g18) = 3.14159
    c: Coincident(g17,g18)
    c: Perpendicular(g16,g15)
    c: Perpendicular(g18,g11)
    c: Distance(g16) = 1.2
    c: Distance(g18) = 1.8
    c: Coincident(g19,g-13)
    c: PointOnObject(g19,g1)
    c: Coincident(g19,g20)
    c: PointOnObject(g20,g5)
    c: Coincident(g20,g21)
    c: Coincident(g21,g-14)
    c: Angle(g21,g20) = 3.14159
    c: Angle(g19,g20) = 3.14159
    c: Perpendicular(g21,g5)
    c: Perpendicular(g1,g19)
    c: Distance(g19) = 1.2
    c: Distance(g21) = 1.8
    c: Coincident(g22,g-16)
    c: Coincident(g22,g23)
    c: Coincident(g23,g24)
    c: Coincident(g24,g-15)
    c: PointOnObject(g25,g-17)
    c: PointOnObject(g25,g-20)
    c: Coincident(g25,g26)
    c: Coincident(g26,g-20)
    c: Coincident(g26,g27)
    c: Coincident(g27,g-19)
    c: Coincident(g27,g28)
    c: PointOnObject(g28,g-19)
    c: Coincident(g28,g29)
    c: PointOnObject(g29,g-18)
    c: Coincident(g29,g30)
    c: Coincident(g30,g-18)
    c: Coincident(g30,g31)
    c: Coincident(g31,g-17)
    c: Coincident(g31,g32)
    c: Coincident(g32,g25)
    c: PointOnObject(g22,g25)
    c: PointOnObject(g23,g29)
    c: Angle(g23,g24) = 3.14159
    c: Angle(g23,g22) = 3.14159
    c: Distance(g22) = 1.2
    c: Distance(g24) = 1.8
    c: Perpendicular(g23,g29)
    c: Perpendicular(g23,g25)
    c: Coincident(g-29,g33)
    c: Coincident(g33,g-30)
    c: Coincident(g33,g34)
    c: PointOnObject(g34,g-30)
    c: Coincident(g34,g35)
    c: PointOnObject(g35,g-27)
    c: Coincident(g35,g36)
    c: Coincident(g36,g-27)
    c: Coincident(g36,g37)
    c: Coincident(g37,g-28)
    c: Coincident(g37,g38)
    c: PointOnObject(g38,g-28)
    c: Coincident(g38,g39)
    c: PointOnObject(g39,g-29)
    c: Coincident(g39,g40)
    c: Coincident(g40,g33)
    c: Coincident(g-32,g41)
    c: PointOnObject(g41,g39)
    c: Coincident(g41,g42)
    c: PointOnObject(g42,g35)
    c: Coincident(g42,g43)
    c: Coincident(g-31,g43)
    c: Angle(g42,g41) = 3.14159
    c: Angle(g43,g42) = 3.14159
    c: Distance(g41) = 1.2
    c: Distance(g42) = 1
    c: Perpendicular(g42,g39)
    c: Perpendicular(g43,g35)
    c: PointOnObject(g44,g-24)
    c: Coincident(g44,g-24)
    c: Coincident(g44,g45)
    c: Coincident(g45,g-25)
    c: Coincident(g45,g46)
    c: PointOnObject(g46,g-25)
    c: Coincident(g46,g47)
    c: PointOnObject(g47,g-22)
    c: Coincident(g47,g48)
    c: Coincident(g48,g49)
    c: Coincident(g49,g-23)
    c: Coincident(g49,g50)
    c: Coincident(g50,g51)
    c: Coincident(g51,g44)
    c: Coincident(g-22,g48)
    c: PointOnObject(g50,g-23)
    c: Coincident(g-26,g52)
    c: PointOnObject(g52,g51)
    c: Coincident(g52,g53)
    c: PointOnObject(g53,g47)
    c: Coincident(g53,g54)
    c: Coincident(g54,g-21)
    c: Angle(g52,g53) = 3.14159
    c: Angle(g54,g53) = 3.14159
    c: Distance(g52) = 1.2
    c: Distance(g53) = 1
    c: Perpendicular(g51,g52)
    c: Perpendicular(g47,g54)
FEATURE [PartDesign::Pocket] Pocket005  label="RChoc sockets"
  BaseFeature = -> Pocket004
  Direction = (-1,2e-16,-3e-16)
  Length = 14.6
  Length2 = 100
  Midplane = true
  Placement = pos=(0,0,0) rot=(0.57735,0.57735,0.57735;2.0944rad)
  Profile = -> Sketch014
  Type = 0
FEATURE [Sketcher::SketchObject] Sketch017
  ExternalGeometry = -> [Sketch012]
  FullyConstrained = true
  MapMode = 5
  Placement = pos=(0,0,0) rot=(0.57735,0.57735,0.57735;2.0944rad)
  Support = -> [YZ_Plane002]
  expr: Constraints[39] = <<Spreadsheet>>.Wiring
  sketch-geometry (16):
    g0: LineSegment StartX=-13.6658 StartY=3.24435 StartZ=0 EndX=-12.6239 EndY=9.15319 EndZ=0
    g1: LineSegment StartX=-12.6239 StartY=9.15319 StartZ=0 EndX=-11.9293 EndY=13.0924 EndZ=0
    g2: LineSegment StartX=-11.9293 StartY=13.0924 StartZ=0 EndX=-9.46385 EndY=12.9848 EndZ=0
    g3: LineSegment StartX=-9.46385 StartY=12.9848 StartZ=0 EndX=-9.11523 EndY=9 EndZ=0
    g4: LineSegment StartX=-9.11523 StartY=9 StartZ=0 EndX=-8.59229 EndY=3.02283 EndZ=0
    g5: LineSegment StartX=-8.59229 StartY=3.02283 StartZ=0 EndX=-8.59229 EndY=0 EndZ=0
    g6: LineSegment StartX=-8.59229 StartY=0 StartZ=0 EndX=-13.6658 EndY=0 EndZ=0
    g7: LineSegment StartX=-13.6658 StartY=0 StartZ=0 EndX=-13.6658 EndY=3.24435 EndZ=0
    g8: LineSegment StartX=15.2934 StartY=0 StartZ=0 EndX=10.3354 EndY=0 EndZ=0
    g9: LineSegment StartX=10.3354 StartY=0 StartZ=0 EndX=10.3354 EndY=4.67879 EndZ=0
    g10: LineSegment StartX=10.3354 StartY=4.67879 StartZ=0 EndX=9.81247 EndY=10.656 EndZ=0
    g11: LineSegment StartX=9.81247 StartY=10.656 StartZ=0 EndX=9.46385 EndY=14.6407 EndZ=0
    g12: LineSegment StartX=9.46385 StartY=14.6407 StartZ=0 EndX=11.8732 EndY=15.1749 EndZ=0
    g13: LineSegment StartX=11.8732 StartY=15.1749 StartZ=0 EndX=13.2412 EndY=11.4161 EndZ=0
    g14: LineSegment StartX=13.2412 StartY=11.4161 StartZ=0 EndX=15.2934 EndY=5.77794 EndZ=0
    g15: LineSegment StartX=15.2934 StartY=5.77794 StartZ=0 EndX=15.2934 EndY=0 EndZ=0
  constraints (40):
    c: Coincident(g0,g-4)
    c: Coincident(g0,g1)
    c: Coincident(g1,g-3)
    c: Coincident(g1,g2)
    c: Coincident(g2,g-3)
    c: Coincident(g2,g3)
    c: Coincident(g3,g-4)
    c: Coincident(g3,g4)
    c: Coincident(g4,g5)
    c: PointOnObject(g5,g-1)
    c: Vertical(g5)
    c: Coincident(g5,g6)
    c: PointOnObject(g6,g-1)
    c: Coincident(g6,g7)
    c: Coincident(g7,g0)
    c: Vertical(g7)
    c: Angle(g4,g3) = 3.14159
    c: Angle(g1,g0) = 3.14159
    c: PointOnObject(g8,g-1)
    c: PointOnObject(g8,g-1)
    c: Coincident(g8,g9)
    c: Vertical(g9)
    c: Coincident(g9,g10)
    c: Coincident(g10,g-6)
    c: Coincident(g10,g11)
    c: Coincident(g11,g-5)
    c: Coincident(g11,g12)
    c: Coincident(g12,g-5)
    c: Coincident(g12,g13)
    c: Coincident(g13,g-6)
    c: Coincident(g13,g14)
    c: Coincident(g14,g15)
    c: Coincident(g15,g8)
    c: Vertical(g15)
    c: Equal(g0,g4)
    c: Equal(g4,g10)
    c: Equal(g10,g14)
    c: Angle(g11,g10) = 3.14159
    c: Angle(g13,g14) = 3.14159
    c: Distance(g0) = 6
FEATURE [PartDesign::Pad] Pad009  label="RInner legs"
  BaseFeature = -> Pocket005
  Direction = (1,-2e-16,3e-16)
  Length = 4.1
  Length2 = 9.5
  Placement = pos=(0,0,0) rot=(0.57735,0.57735,0.57735;2.0944rad)
  Profile = -> Sketch017
  Type = 4
  expr: Length = <<Spreadsheet>>.ScrewD / 2 + 2mm
FEATURE [Sketcher::SketchObject] Sketch018
  ExternalGeometry = -> [Sketch012]
  FullyConstrained = true
  MapMode = 5
  Placement = pos=(0,0,0) rot=(0.57735,0.57735,0.57735;2.0944rad)
  Support = -> [YZ_Plane002]
  expr: Constraints[53] = <<Spreadsheet>>.ArchLength
  expr: Constraints[54] = <<Spreadsheet>>.ArchLength - 5mm
  expr: Constraints[56] = <<Spreadsheet>>.ArchLength - 10mm
  expr: Constraints[57] = <<Spreadsheet>>.ArchLength
  expr: Constraints[58] = <<Spreadsheet>>.ArchLength - 5mm
  expr: Constraints[73] = <<Spreadsheet>>.ArchLength - 10mm
  sketch-geometry (36):
    g0: LineSegment StartX=-37.2204 StartY=8.07075 StartZ=0 EndX=-34.6847 EndY=13.5086 EndZ=0
    g1: LineSegment StartX=-34.6847 StartY=13.5086 StartZ=0 EndX=-32.9942 EndY=17.1338 EndZ=0
    g2: LineSegment StartX=-32.9942 StartY=17.1338 StartZ=0 EndX=-30.6407 EndY=16.3917 EndZ=0
    g3: LineSegment StartX=-30.6407 StartY=16.3917 StartZ=0 EndX=-31.3353 EndY=12.4525 EndZ=0
    g4: LineSegment StartX=-31.3353 StartY=12.4525 StartZ=0 EndX=-32.3771 EndY=6.54366 EndZ=0
    g5: LineSegment StartX=33.1475 StartY=12.2763 StartZ=0 EndX=31.0954 EndY=17.9145 EndZ=0
    g6: LineSegment StartX=31.0954 StartY=17.9145 StartZ=0 EndX=29.7273 EndY=21.6733 EndZ=0
    g7: LineSegment StartX=29.7273 StartY=21.6733 StartZ=0 EndX=31.9163 EndY=22.8128 EndZ=0
    g8: LineSegment StartX=31.9163 StartY=22.8128 StartZ=0 EndX=34.2106 EndY=19.5362 EndZ=0
    g9: LineSegment StartX=34.2106 StartY=19.5362 StartZ=0 EndX=37.6521 EndY=14.6212 EndZ=0
    g10: LineSegment StartX=-37.2204 StartY=8.07075 StartZ=0 EndX=-39.0097 EndY=4.23371 EndZ=0
    g11: LineSegment StartX=-39.0097 StartY=4.23371 StartZ=0 EndX=-39.0097 EndY=0 EndZ=0
    g12: LineSegment StartX=37.6521 StartY=14.6212 StartZ=0 EndX=42.2621 EndY=8.03739 EndZ=0
    g13: LineSegment StartX=42.2621 StartY=8.03739 StartZ=0 EndX=42.2621 EndY=0 EndZ=0
    g14: LineSegment StartX=-32.3771 StartY=6.54366 StartZ=0 EndX=-35 EndY=0 EndZ=0
    g15: LineSegment StartX=-35 StartY=0 StartZ=0 EndX=-45 EndY=0 EndZ=0
    g16: LineSegment StartX=-45 StartY=0 StartZ=0 EndX=-45 EndY=3 EndZ=0
    g17: LineSegment StartX=-45 StartY=3 StartZ=0 EndX=-40 EndY=3 EndZ=0
    g18: LineSegment StartX=40 StartY=3 StartZ=0 EndX=45 EndY=3 EndZ=0
    g19: LineSegment StartX=45 StartY=3 StartZ=0 EndX=45 EndY=0 EndZ=0
    g20: LineSegment StartX=45 StartY=0 StartZ=0 EndX=35 EndY=0 EndZ=0
    g21: LineSegment StartX=35 StartY=0 StartZ=0 EndX=33.1475 EndY=12.2763 EndZ=0
    g22-g25: Circle x4 (B-spline internal-alignment scaffolding for g26; pole/knot coordinates omitted)
    g26: BSplineCurve PolesCount=4 KnotsCount=2 Degree=3 IsPeriodic=0
    g27: GeomPoint X=-37.2204 Y=8.07075 Z=0
    g28: GeomPoint X=-45 Y=3 Z=0
    g29-g32: Circle x4 (B-spline internal-alignment scaffolding for g33; pole/knot coordinates omitted)
    g33: BSplineCurve PolesCount=4 KnotsCount=2 Degree=3 IsPeriodic=0
    g34: GeomPoint X=37.6521 Y=14.6212 Z=0
    g35: GeomPoint X=45 Y=3 Z=0
  constraints (82):
    c: Coincident(g0,g-6)
    c: Coincident(g0,g1)
    c: Coincident(g1,g-5)
    c: Coincident(g1,g2)
    c: Coincident(g2,g-5)
    c: Coincident(g2,g3)
    c: Coincident(g3,g-6)
    c: Coincident(g3,g4)
    c: Coincident(g5,g-3)
    c: Coincident(g5,g6)
    c: Coincident(g6,g-4)
    c: Coincident(g6,g7)
    c: Coincident(g7,g-4)
    c: Coincident(g7,g8)
    c: Coincident(g8,g-3)
    c: Coincident(g8,g9)
    c: Angle(g9,g8) = 3.14159
    c: Angle(g5,g6) = 3.14159
    c: Distance(g9) = 6
    c: Equal(g9,g5)
    c: Equal(g5,g4)
    c: Equal(g4,g0)
    c: Angle(g3,g4) = 3.14159
    c: Angle(g1,g0) = 3.14159
    c: Coincident(g10,g0)
    c: Coincident(g11,g10)
    c: PointOnObject(g11,g-1)
    c: Vertical(g11)
    c: Coincident(g12,g9)
    c: Coincident(g13,g12)
    c: PointOnObject(g13,g-1)
    c: Vertical(g13)
    c: Equal(g12,g13)
    c: Equal(g10,g11)
    c: Angle(g0,g10) = 3.14159
    c: Angle(g12,g9) = 3.14159
    c: Coincident(g4,g14)
    c: PointOnObject(g14,g-1)
    c: Coincident(g14,g15)
    c: PointOnObject(g15,g-1)
    c: Coincident(g15,g16)
    c: Vertical(g16)
    c: DistanceY(g16,g16) = 3
    c: Coincident(g17,g16)
    c: Horizontal(g17)
    c: Horizontal(g18)
    c: Coincident(g18,g19)
    c: PointOnObject(g19,g-1)
    c: Vertical(g19)
    c: Coincident(g19,g20)
    c: PointOnObject(g20,g-1)
    c: Coincident(g20,g21)
    c: Coincident(g21,g5)
    c: DistanceX(g-7,g19) = 45
    c: DistanceX(g-7,g18) = 40
    c: Equal(g19,g16)
    c: DistanceX(g14,g-7) = 35
    c: DistanceX(g16,g-7) = 45
    c: DistanceX(g17,g-7) = 40
    c: Coincident(g26,g0)
    c: Weight(g22) = 1
    c: Equal(g22,g23)
    c: Coincident(g23,g10)
    c: Equal(g22,g24)
    c: Coincident(g24,g17)
    c: Equal(g22,g25)
    c: Coincident(g26,g16)
    c: InternalAlignment(g22-g25 -> g26) x4
    c: InternalAlignment(g27,g26)
    c: InternalAlignment(g28,g26)
    c: DistanceX(g-7,g20) = 35
    c: Coincident(g33,g9)
    c: Weight(g29) = 1
    c: Equal(g29,g30)
    c: Coincident(g30,g12)
    c: Equal(g29,g31)
    c: Coincident(g31,g18)
    c: Equal(g29,g32)
    c: Coincident(g33,g19)
    c: InternalAlignment(g29-g32 -> g33) x4
    c: InternalAlignment(g34,g33)
    c: InternalAlignment(g35,g33)
FEATURE [PartDesign::Pad] Pad010  label="ROuter Legs"
  BaseFeature = -> Pad009
  Direction = (1,-2e-16,3e-16)
  Length = 9.5
  Length2 = 100
  Placement = pos=(0,0,0) rot=(0.57735,0.57735,0.57735;2.0944rad)
  Profile = -> Sketch018
  Reversed = true
  Type = 0
FEATURE [Sketcher::SketchObject] Sketch019
  ExternalGeometry = -> [Sketch018]
  FullyConstrained = true
  MapMode = 5
  Support = -> [XY_Plane002]
  expr: Constraints[15] = <<Spreadsheet>>.NutR
  expr: Constraints[16] = <<Spreadsheet>>.NutR
  expr: Constraints[28] = <<Spreadsheet>>.ScrewD
  expr: Constraints[53] = <<Spreadsheet>>.NutR
  expr: Constraints[54] = <<Spreadsheet>>.NutR
  expr: Constraints[57] = <<Spreadsheet>>.ScrewD
  sketch-geometry (22):
    g0: LineSegment StartX=7.6225 StartY=46.0949 StartZ=0 EndX=0 EndY=40 EndZ=0
    g1: LineSegment StartX=0 StartY=40 StartZ=0 EndX=1e-14 EndY=45 EndZ=0
    g2: LineSegment StartX=1e-14 StartY=45 StartZ=0 EndX=-9.5 EndY=45 EndZ=0
    g3: LineSegment StartX=-9.5 StartY=45 StartZ=0 EndX=-9.5 EndY=55 EndZ=0
    g4: LineSegment StartX=-9.5 StartY=55 StartZ=0 EndX=4.5 EndY=55 EndZ=0
    g5: ArcOfCircle CenterX=4.5 CenterY=50 CenterZ=0 NormalX=0 NormalY=0 NormalZ=1 AngleXU=0 Radius=5 StartAngle=5.38688 EndAngle=7.85398
    g6: LineSegment StartX=4.5 StartY=50 StartZ=0 EndX=0 EndY=50 EndZ=0
    g7: Circle CenterX=0 CenterY=50 CenterZ=0 NormalX=0 NormalY=0 NormalZ=1 AngleXU=0 Radius=2.1
    g8: LineSegment StartX=9.5 StartY=50 StartZ=0 EndX=9.5 EndY=55 EndZ=0
    g9: LineSegment StartX=9.5 StartY=55 StartZ=0 EndX=0 EndY=50 EndZ=0
    g10: LineSegment StartX=-9.5 StartY=55 StartZ=0 EndX=0 EndY=50 EndZ=0
    g11: LineSegment StartX=-1.07e-14 StartY=-45 StartZ=0 EndX=0 EndY=-40 EndZ=0
    g12: LineSegment StartX=0 StartY=-40 StartZ=0 EndX=7.6225 EndY=-46.0949 EndZ=0
    g13: ArcOfCircle CenterX=4.5 CenterY=-50 CenterZ=0 NormalX=0 NormalY=0 NormalZ=1 AngleXU=0 Radius=5 StartAngle=4.71239 EndAngle=7.17949
    g14: LineSegment StartX=4.5 StartY=-55 StartZ=0 EndX=-9.5 EndY=-55 EndZ=0
    g15: LineSegment StartX=-9.5 StartY=-55 StartZ=0 EndX=-9.5 EndY=-45 EndZ=0
    g16: LineSegment StartX=-9.5 StartY=-45 StartZ=0 EndX=-1.07e-14 EndY=-45 EndZ=0
    g17: LineSegment StartX=-9.5 StartY=-55 StartZ=0 EndX=0 EndY=-50 EndZ=0
    g18: LineSegment StartX=0 StartY=-50 StartZ=0 EndX=9.5 EndY=-55 EndZ=0
    g19: LineSegment StartX=9.5 StartY=-55 StartZ=0 EndX=9.5 EndY=-50 EndZ=0
    g20: LineSegment StartX=4.5 StartY=-50 StartZ=0 EndX=0 EndY=-50 EndZ=0
    g21: Circle CenterX=0 CenterY=-50 CenterZ=0 NormalX=0 NormalY=0 NormalZ=1 AngleXU=0 Radius=2.1
  constraints (58):
    c: PointOnObject(g0,g-2)
    c: Coincident(g0,g1)
    c: Coincident(g1,g-3)
    c: Coincident(g1,g2)
    c: Horizontal(g2)
    c: Coincident(g2,g3)
    c: Vertical(g3)
    c: Coincident(g3,g4)
    c: Horizontal(g4)
    c: Tangent(g4,g5) = 1.5708
    c: Tangent(g5,g0) = 1.5708
    c: Coincident(g6,g5)
    c: PointOnObject(g6,g-2)
    c: Horizontal(g6)
    c: Coincident(g7,g6)
    c: DistanceY(g7,g3) = 5
    c: DistanceY(g2,g7) = 5
    c: PointOnObject(g8,g5)
    c: Vertical(g8)
    c: Horizontal(g8,g5)
    c: Coincident(g9,g8)
    c: Coincident(g9,g7)
    c: Coincident(g10,g3)
    c: Coincident(g10,g7)
    c: Equal(g10,g9)
    c: Horizontal(g8,g4)
    c: DistanceX(g3,g8) = 19
    c: DistanceY(g1,g1) = 5
    c: Diameter(g7) = 4.2
    c: Coincident(g11,g-4)
    c: PointOnObject(g11,g-2)
    c: Coincident(g11,g12)
    c: Tangent(g12,g13) = 1.5708
    c: Tangent(g13,g14) = 1.5708
    c: Coincident(g14,g15)
    c: Vertical(g15)
    c: Coincident(g15,g16)
    c: Coincident(g16,g11)
    c: Horizontal(g16)
    c: Horizontal(g14)
    c: Equal(g11,g1)
    c: Coincident(g14,g17)
    c: PointOnObject(g17,g-2)
    c: Coincident(g17,g18)
    c: Coincident(g18,g19)
    c: PointOnObject(g19,g13)
    c: Vertical(g19)
    c: Coincident(g20,g13)
    c: Horizontal(g20)
    c: Coincident(g17,g20)
    c: Horizontal(g18,g13)
    c: DistanceX(g14,g18) = 19
    c: Equal(g18,g17)
    c: DistanceY(g17,g15) = 5
    c: DistanceY(g14,g17) = 5
    c: Horizontal(g19,g13)
    c: Coincident(g21,g17)
    c: Diameter(g21) = 4.2
FEATURE [PartDesign::Pad] Pad011  label="RFeet"
  BaseFeature = -> Pad010
  Direction = (0,0,1)
  Length = 3
  Length2 = 100
  Placement = pos=(0,0,0) rot=(0.57735,0.57735,0.57735;2.0944rad)
  Profile = -> Sketch019
  Type = 0
FEATURE [PartDesign::Body] Body002  label="RingArch"
  Group = -> [Sketch012,Pad008,Sketch013,Pocket004,Sketch014,Pocket005,Sketch017,Pad009,Sketch018,Pad010,Sketch019,Pad011]
  Origin = -> Origin002
  Placement = pos=(50,0,5) rot=(0,0,1;0rad)
  Tip = -> Pad011
COMPONENT P3 — recipe-attached ("MiddleArch", modeled in this document).
Construction recipe (the document's own serialized feature program — sketch geometry with constraints, then the solid features built on it; lengths are millimeters unless a unit is written):

FEATURE [Sketcher::SketchObject] Sketch020
  FullyConstrained = true
  MapMode = 5
  Placement = pos=(0,0,0) rot=(0.57735,0.57735,0.57735;2.0944rad)
  Support = -> [YZ_Plane003]
  expr: Constraints[114] = <<Spreadsheet>>.ARowKey
  expr: Constraints[115] = <<Spreadsheet>>.ZRowKey
  expr: Constraints[134] = <<Spreadsheet>>.QRowKey
  expr: Constraints[153] = <<Spreadsheet>>.TopRowKey
  expr: Constraints[172] = <<Spreadsheet>>.Wiring
  expr: Constraints[90] = <<Spreadsheet>>.ModRowKey
  sketch-geometry (62):
    g0: LineSegment StartX=-50.2141 StartY=25.1636 StartZ=0 EndX=-41.6042 EndY=21.1487 EndZ=0
    g1: LineSegment StartX=-41.6042 StartY=21.1487 StartZ=0 EndX=-32.9942 EndY=17.1338 EndZ=0
    g2: LineSegment StartX=-32.9942 StartY=17.1338 StartZ=0 EndX=-30.6407 EndY=16.3917 EndZ=0
    g3: LineSegment StartX=-30.6407 StartY=16.3917 StartZ=0 EndX=-21.285 EndY=14.7421 EndZ=0
    g4: LineSegment StartX=-21.285 StartY=14.7421 StartZ=0 EndX=-11.9293 EndY=13.0924 EndZ=0
    g5: LineSegment StartX=-11.9293 StartY=13.0924 StartZ=0 EndX=-9.46385 EndY=12.9848 EndZ=0
    g6: LineSegment StartX=-9.46385 StartY=12.9848 StartZ=0 EndX=0 EndY=13.8128 EndZ=0
    g7: LineSegment StartX=-1e-16 StartY=13.8128 StartZ=0 EndX=9.46385 EndY=14.6407 EndZ=0
    g8: LineSegment StartX=9.46385 StartY=14.6407 StartZ=0 EndX=11.8732 EndY=15.1749 EndZ=0
    g9: LineSegment StartX=11.8732 StartY=15.1749 StartZ=0 EndX=20.8002 EndY=18.4241 EndZ=0
    g10: LineSegment StartX=20.8002 StartY=18.4241 StartZ=0 EndX=29.7273 EndY=21.6733 EndZ=0
    g11: LineSegment StartX=29.7273 StartY=21.6733 StartZ=0 EndX=31.9163 EndY=22.8128 EndZ=0
    g12: LineSegment StartX=31.9163 StartY=22.8128 StartZ=0 EndX=39.6982 EndY=28.2617 EndZ=0
    g13: LineSegment StartX=39.6982 StartY=28.2617 StartZ=0 EndX=47.4802 EndY=33.7107 EndZ=0
    g14: LineSegment StartX=47.4802 StartY=33.7107 StartZ=0 EndX=49.7745 EndY=30.4341 EndZ=0
    g15: LineSegment StartX=49.7745 StartY=30.4341 StartZ=0 EndX=34.2106 EndY=19.5362 EndZ=0
    g16: LineSegment StartX=34.2106 StartY=19.5362 StartZ=0 EndX=31.0954 EndY=17.9145 EndZ=0
    g17: LineSegment StartX=31.0954 StartY=17.9145 StartZ=0 EndX=13.2412 EndY=11.4161 EndZ=0
    g18: LineSegment StartX=13.2412 StartY=11.4161 StartZ=0 EndX=9.81247 EndY=10.656 EndZ=0
    g19: LineSegment StartX=9.81247 StartY=10.656 StartZ=0 EndX=-9.11523 EndY=9 EndZ=0
    g20: LineSegment StartX=-9.11523 StartY=9 StartZ=0 EndX=-12.6239 EndY=9.15319 EndZ=0
    g21: LineSegment StartX=-12.6239 StartY=9.15319 StartZ=0 EndX=-31.3353 EndY=12.4525 EndZ=0
    g22: LineSegment StartX=-31.3353 StartY=12.4525 StartZ=0 EndX=-34.6847 EndY=13.5086 EndZ=0
    g23: LineSegment StartX=-34.6847 StartY=13.5086 StartZ=0 EndX=-51.9046 EndY=21.5383 EndZ=0
    g24: LineSegment StartX=-51.9046 StartY=21.5383 StartZ=0 EndX=-50.2141 EndY=25.1636 EndZ=0
    g25: LineSegment StartX=-32.9942 StartY=17.1338 StartZ=0 EndX=-34.6847 EndY=13.5086 EndZ=0
    g26: LineSegment StartX=-31.3353 StartY=12.4525 StartZ=0 EndX=-30.6407 EndY=16.3917 EndZ=0
    g27: LineSegment StartX=-11.9293 StartY=13.0924 StartZ=0 EndX=-12.6239 EndY=9.15319 EndZ=0
    g28: LineSegment StartX=-9.11523 StartY=9 StartZ=0 EndX=-9.46385 EndY=12.9848 EndZ=0
    g29: LineSegment StartX=9.46385 StartY=14.6407 StartZ=0 EndX=9.81247 EndY=10.656 EndZ=0
    g30: LineSegment StartX=13.2412 StartY=11.4161 StartZ=0 EndX=11.8732 EndY=15.1749 EndZ=0
    g31: LineSegment StartX=29.7273 StartY=21.6733 StartZ=0 EndX=31.0954 EndY=17.9145 EndZ=0
    g32: LineSegment StartX=34.2106 StartY=19.5362 StartZ=0 EndX=31.9163 EndY=22.8128 EndZ=0
    g33: LineSegment StartX=36.8304 StartY=32.3575 StartZ=0 EndX=34.3729 EndY=30.6368 EndZ=0
    g34: LineSegment StartX=34.3729 StartY=30.6368 StartZ=0 EndX=28.6371 EndY=38.8283 EndZ=0
    g35: LineSegment StartX=18.489 StartY=33.5455 StartZ=0 EndX=21.9092 EndY=24.1486 EndZ=0
    g36: LineSegment StartX=21.9092 StartY=24.1486 StartZ=0 EndX=19.0901 EndY=23.1225 EndZ=0
    g37: LineSegment StartX=19.0901 StartY=23.1225 StartZ=0 EndX=16.2711 EndY=22.0965 EndZ=0
    g38: LineSegment StartX=16.2711 StartY=22.0965 StartZ=0 EndX=12.8509 EndY=31.4934 EndZ=0
    g39: LineSegment StartX=1.68125 StartY=29.0171 StartZ=0 EndX=2.55281 EndY=19.0552 EndZ=0
    g40: LineSegment StartX=2.55281 StartY=19.0552 StartZ=0 EndX=-0.435779 EndY=18.7937 EndZ=0
    g41: LineSegment StartX=-3.42436 StartY=18.5323 StartZ=0 EndX=-0.435779 EndY=18.7937 EndZ=0
    g42: LineSegment StartX=-15.7258 StartY=28.9933 StartZ=0 EndX=-17.4623 EndY=19.1452 EndZ=0
    g43: LineSegment StartX=-17.4623 StartY=19.1452 StartZ=0 EndX=-20.4167 EndY=19.6661 EndZ=0
    g44: LineSegment StartX=-20.4167 StartY=19.6661 StartZ=0 EndX=-23.3712 EndY=20.1871 EndZ=0
    g45: LineSegment StartX=-23.3712 StartY=20.1871 StartZ=0 EndX=-21.6347 EndY=30.0351 EndZ=0
    g46: LineSegment StartX=-32.546 StartY=33.4755 StartZ=0 EndX=-36.7722 EndY=24.4124 EndZ=0
    g47: LineSegment StartX=-36.7722 StartY=24.4124 StartZ=0 EndX=-39.4911 EndY=25.6802 EndZ=0
    g48: LineSegment StartX=-39.4911 StartY=25.6802 StartZ=0 EndX=-41.6042 EndY=21.1487 EndZ=0
    g49: LineSegment StartX=-20.4167 StartY=19.6661 StartZ=0 EndX=-21.285 EndY=14.7421 EndZ=0
    g50: LineSegment StartX=-0.435779 StartY=18.7937 StartZ=0 EndX=-1e-16 EndY=13.8128 EndZ=0
    g51: LineSegment StartX=20.8002 StartY=18.4241 StartZ=0 EndX=19.0901 EndY=23.1225 EndZ=0
    g52: ArcOfCircle CenterX=-14.0244 CenterY=73.195 CenterZ=0 NormalX=0 NormalY=0 NormalZ=1 AngleXU=0 Radius=43.8257 StartAngle=4.27606 EndAngle=4.53786
    g53: ArcOfCircle CenterX=-2.13841 CenterY=72.6761 CenterZ=0 NormalX=0 NormalY=0 NormalZ=1 AngleXU=0 Radius=43.8257 StartAngle=4.79966 EndAngle=5.06145
    g54: ArcOfCircle CenterX=3.49974 CenterY=74.7282 CenterZ=0 NormalX=0 NormalY=0 NormalZ=1 AngleXU=0 Radius=43.8257 StartAngle=5.06145 EndAngle=5.32325
    g55: LineSegment StartX=-3.42436 StartY=18.5323 StartZ=0 EndX=-4.29592 EndY=28.4942 EndZ=0
    g56: ArcOfCircle CenterX=-8.11558 CenterY=72.1532 CenterZ=0 NormalX=0 NormalY=0 NormalZ=1 AngleXU=0 Radius=43.8257 StartAngle=4.53786 EndAngle=4.79966
    g57: LineSegment StartX=36.8304 StartY=32.3575 StartZ=0 EndX=39.6982 EndY=28.2617 EndZ=0
    g58: LineSegment StartX=-50 StartY=3 StartZ=0 EndX=-70 EndY=3 EndZ=0
    g59: LineSegment StartX=-50 StartY=0 StartZ=0 EndX=-50 EndY=3 EndZ=0
    g60: LineSegment StartX=-50 StartY=3 StartZ=0 EndX=-50 EndY=9 EndZ=0
    g61: LineSegment StartX=-50 StartY=9 StartZ=0 EndX=50 EndY=9 EndZ=0
  constraints (179):
    c: Coincident(g0,g1)
    c: Coincident(g1,g2)
    c: Coincident(g2,g3)
    c: Coincident(g3,g4)
    c: Coincident(g4,g5)
    c: Coincident(g5,g6)
    c: Coincident(g8,g9)
    c: Coincident(g9,g10)
    c: Coincident(g10,g11)
    c: Coincident(g11,g12)
    c: Coincident(g13,g14)
    c: Coincident(g14,g15)
    c: Coincident(g15,g16)
    c: Coincident(g16,g17)
    c: Coincident(g17,g18)
    c: Coincident(g18,g19)
    c: Coincident(g19,g20)
    c: Coincident(g20,g21)
    c: Coincident(g21,g22)
    c: Coincident(g22,g23)
    c: Coincident(g23,g24)
    c: Coincident(g24,g0)
    c: Coincident(g25,g1)
    c: Coincident(g25,g22)
    c: Coincident(g26,g21)
    c: Coincident(g26,g2)
    c: Coincident(g27,g4)
    c: Coincident(g27,g20)
    c: Coincident(g28,g19)
    c: Coincident(g28,g5)
    c: Coincident(g29,g18)
    c: Coincident(g30,g17)
    c: Coincident(g30,g8)
    c: Coincident(g31,g10)
    c: Coincident(g31,g16)
    c: Coincident(g32,g15)
    c: Coincident(g32,g11)
    c: Coincident(g33,g34)
    c: Coincident(g35,g36)
    c: Coincident(g36,g37)
    c: Coincident(g37,g38)
    c: Coincident(g39,g40)
    c: Coincident(g42,g43)
    c: Coincident(g43,g44)
    c: Coincident(g44,g45)
    c: Coincident(g46,g47)
    c: Coincident(g47,g48)
    c: Coincident(g48,g0)
    c: Coincident(g49,g3)
    c: Coincident(g50,g40)
    c: Coincident(g50,g6)
    c: Coincident(g51,g9)
    c: Coincident(g51,g36)
    c: Coincident(g7,g29)
    c: Coincident(g49,g43)
    c: Coincident(g52,g46)
    c: Coincident(g52,g45)
    c: Coincident(g53,g39)
    c: Coincident(g53,g38)
    c: Perpendicular(g43,g42)
    c: Parallel(g3,g4)
    c: Equal(g1,g0)
    c: Perpendicular(g1,g48)
    c: Parallel(g1,g0)
    c: Distance(g47,g43) = 20
    c: Perpendicular(g4,g49)
    c: Perpendicular(g49,g43)
    c: Coincident(g7,g6)
    c: Coincident(g41,g40)
    c: Parallel(g13,g12)
    c: Distance(g36,g40) = 20
    c: Distance(g19) = 19
    c: Distance(g40,g43) = 20
    c: Equal(g4,g3)
    c: Perpendicular(g6,g50)
    c: Parallel(g7,g6)
    c: Equal(g6,g7)
    c: Coincident(g55,g41)
    c: Coincident(g56,g42)
    c: Coincident(g56,g55)
    c: Perpendicular(g49,g44)
    c: Perpendicular(g1,g25)
    c: Perpendicular(g23,g25)
    c: Perpendicular(g23,g24)
    c: Equal(g23,g21)
    c: Equal(g19,g21)
    c: Perpendicular(g26,g3)
    c: Perpendicular(g21,g27)
    c: Perpendicular(g27,g4)
    c: Perpendicular(g29,g7)
    c: Distance(g48) = 5
    c: Distance(g46) = 10
    c: Distance(g45) = 10
    c: Equal(g44,g43)
    c: Equal(g41,g43)
    c: Equal(g40,g41)
    c: Equal(g37,g36)
    c: Equal(g36,g40)
    c: Equal(g36,g33)
    c: Perpendicular(g51,g36)
    c: Perpendicular(g51,g37)
    c: Perpendicular(g50,g40)
    c: Perpendicular(g52,g45)
    c: Perpendicular(g52,g46)
    c: Equal(g26,g25)
    c: Perpendicular(g45,g44)
    c: Perpendicular(g47,g46)
    c: Perpendicular(g48,g47)
    c: Equal(g28,g27)
    c: Perpendicular(g6,g28)
    c: Distance(g28) = 4
    c: Distance(g42) = 10
    c: Distance(g55) = 10
    c: Distance(g39) = 10
    c: Distance(g50) = 5
    c: Distance(g49) = 5
    c: Perpendicular(g56,g42)
    c: Equal(g47,g44)
    c: Distance(g41) = 3
    c: Perpendicular(g50,g41)
    c: Perpendicular(g41,g55)
    c: Perpendicular(g56,g55)
    c: Perpendicular(g40,g39)
    c: Perpendicular(g19,g29)
    c: Coincident(g8,g7)
    c: Parallel(g9,g10)
    c: Equal(g9,g10)
    c: Equal(g17,g19)
    c: Perpendicular(g17,g31)
    c: Perpendicular(g17,g30)
    c: Perpendicular(g9,g30)
    c: Equal(g29,g30)
    c: Perpendicular(g51,g9)
    c: Distance(g38) = 10
    c: Distance(g51) = 5
    c: Perpendicular(g37,g38)
    c: Distance(g35) = 10
    c: Coincident(g35,g54)
    c: Perpendicular(g54,g35)
    c: Coincident(g34,g54)
    c: Perpendicular(g54,g34)
    c: Perpendicular(g34,g33)
    c: Coincident(g57,g33)
    c: Coincident(g57,g12)
    c: Perpendicular(g14,g15)
    c: Equal(g32,g31)
    c: Coincident(g13,g12)
    c: Equal(g12,g13)
    c: Perpendicular(g13,g14)
    c: Perpendicular(g33,g57)
    c: Perpendicular(g12,g32)
    c: Equal(g15,g17)
    c: Distance(g34) = 10
    c: Distance(g57) = 5
    c: Distance(g36,g33) = 20
    c: Perpendicular(g36,g35)
    c: Perpendicular(g53,g38)
    c: Perpendicular(g53,g39)
    c: Perpendicular(g57,g12)
    c: Angle(g51,g57) = 0.261799
    c: Angle(g50,g51) = 0.261799
    c: Angle(g49,g50) = 0.261799
    c: Angle(g48,g49) = 0.261799
    c: Angle(g58,g50) = 1.65806
    c: Horizontal(g58)
    c: PointOnObject(g59,g-1)
    c: Vertical(g59)
    c: Coincident(g60,g59)
    c: Vertical(g60)
    c: Coincident(g61,g60)
    c: Horizontal(g61)
    c: Coincident(g58,g59)
    c: DistanceY(g60,g60) = 6
    c: DistanceY(g59,g59) = 3
    c: DistanceX(g58,g58) = 20
    c: DistanceX(g61,g61) = 100
    c: DistanceX(g59,g-1) = 50
    c: PointOnObject(g6,g-2)
    c: PointOnObject(g19,g61)
FEATURE [PartDesign::Pad] Pad012  label="MArch"
  Direction = (1,-2e-16,3e-16)
  Length = 19
  Length2 = 100
  Midplane = true
  Placement = pos=(0,0,0) rot=(0.57735,0.57735,0.57735;2.0944rad)
  Profile = -> Sketch020
  Type = 0
FEATURE [Sketcher::SketchObject] Sketch021
  ExternalGeometry = -> [Sketch020]
  FullyConstrained = true
  MapMode = 5
  Placement = pos=(0,0,0) rot=(0.57735,0.57735,0.57735;2.0944rad)
  Support = -> [YZ_Plane003]
  sketch-geometry (75):
    g0: LineSegment StartX=-47.9483 StartY=24.107 StartZ=0 EndX=-41.6042 EndY=21.1487 EndZ=0
    g1: LineSegment StartX=-41.6042 StartY=21.1487 StartZ=0 EndX=-35.26 EndY=18.1904 EndZ=0
    g2: LineSegment StartX=-35.26 StartY=18.1904 StartZ=0 EndX=-35.8517 EndY=16.9215 EndZ=0
    g3: LineSegment StartX=-35.8517 StartY=16.9215 StartZ=0 EndX=-34.6735 EndY=16.3721 EndZ=0
    g4: LineSegment StartX=-34.6735 StartY=16.3721 StartZ=0 EndX=-35.7723 EndY=14.0157 EndZ=0
    g5: LineSegment StartX=-50.817 StartY=21.0312 StartZ=0 EndX=-49.7182 EndY=23.3876 EndZ=0
    g6: LineSegment StartX=-49.7182 StartY=23.3876 StartZ=0 EndX=-48.54 EndY=22.8382 EndZ=0
    g7: LineSegment StartX=-48.54 StartY=22.8382 StartZ=0 EndX=-47.9483 EndY=24.107 EndZ=0
    g8: LineSegment StartX=-35.8517 StartY=16.9215 StartZ=0 EndX=-36.9505 EndY=14.5651 EndZ=0
    g9: LineSegment StartX=-48.54 StartY=22.8382 StartZ=0 EndX=-49.6388 EndY=20.4818 EndZ=0
    g10: LineSegment StartX=-49.7182 StartY=23.3876 StartZ=0 EndX=-49.1265 EndY=24.6564 EndZ=0
    g11: LineSegment StartX=-34.6735 StartY=16.3721 StartZ=0 EndX=-34.0818 EndY=17.641 EndZ=0
    g12: LineSegment StartX=-50.817 StartY=21.0312 StartZ=0 EndX=-43.2946 EndY=17.5235 EndZ=0
    g13: LineSegment StartX=-43.2946 StartY=17.5235 StartZ=0 EndX=-35.7723 EndY=14.0157 EndZ=0
    g14: LineSegment StartX=-41.6042 StartY=21.1487 StartZ=0 EndX=-43.2946 EndY=17.5235 EndZ=0
    g15: LineSegment StartX=-30.1535 StartY=12.2441 StartZ=0 EndX=-29.702 EndY=14.8046 EndZ=0
    g16: LineSegment StartX=-29.702 StartY=14.8046 StartZ=0 EndX=-28.4217 EndY=14.5789 EndZ=0
    g17: LineSegment StartX=-28.4217 StartY=14.5789 StartZ=0 EndX=-28.1786 EndY=15.9576 EndZ=0
    g18: LineSegment StartX=-28.1786 StartY=15.9576 StartZ=0 EndX=-21.285 EndY=14.7421 EndZ=0
    g19: LineSegment StartX=-21.285 StartY=14.7421 StartZ=0 EndX=-14.3913 EndY=13.5265 EndZ=0
    g20: LineSegment StartX=-14.3913 StartY=13.5265 StartZ=0 EndX=-14.6344 EndY=12.1478 EndZ=0
    g21: LineSegment StartX=-14.6344 StartY=12.1478 StartZ=0 EndX=-13.3542 EndY=11.9221 EndZ=0
    g22: LineSegment StartX=-13.3542 StartY=11.9221 StartZ=0 EndX=-13.8057 EndY=9.36157 EndZ=0
    g23: LineSegment StartX=-13.8057 StartY=9.36157 StartZ=0 EndX=-21.9796 EndY=10.8028 EndZ=0
    g24: LineSegment StartX=-21.9796 StartY=10.8028 StartZ=0 EndX=-30.1535 EndY=12.2441 EndZ=0
    g25: LineSegment StartX=-29.702 StartY=14.8046 StartZ=0 EndX=-29.4589 EndY=16.1834 EndZ=0
    g26: LineSegment StartX=-21.285 StartY=14.7421 StartZ=0 EndX=-21.9796 EndY=10.8028 EndZ=0
    g27: LineSegment StartX=-13.3542 StartY=11.9221 StartZ=0 EndX=-13.1111 EndY=13.3008 EndZ=0
    g28: LineSegment StartX=-14.6344 StartY=12.1478 StartZ=0 EndX=-15.0859 EndY=9.58731 EndZ=0
    g29: LineSegment StartX=-28.8732 StartY=12.0184 StartZ=0 EndX=-28.4217 EndY=14.5789 EndZ=0
    g30: LineSegment StartX=-8.1464 StartY=11.6947 StartZ=0 EndX=-6.85134 EndY=11.808 EndZ=0
    g31: LineSegment StartX=-6.85134 StartY=11.808 StartZ=0 EndX=-6.97336 EndY=13.2027 EndZ=0
    g32: LineSegment StartX=-6.97336 StartY=13.2027 StartZ=0 EndX=0 EndY=13.8128 EndZ=0
    g33: LineSegment StartX=0 StartY=13.8128 StartZ=0 EndX=6.97336 EndY=14.4228 EndZ=0
    g34: LineSegment StartX=6.97336 StartY=14.4228 StartZ=0 EndX=7.09538 EndY=13.0282 EndZ=0
    g35: LineSegment StartX=7.09538 StartY=13.0282 StartZ=0 EndX=8.39043 EndY=13.1415 EndZ=0
    g36: LineSegment StartX=8.39043 StartY=13.1415 StartZ=0 EndX=8.61704 EndY=10.5514 EndZ=0
    g37: LineSegment StartX=8.61704 StartY=10.5514 StartZ=0 EndX=0.348623 EndY=9.82798 EndZ=0
    g38: LineSegment StartX=0.348623 StartY=9.82798 StartZ=0 EndX=-7.91979 EndY=9.10459 EndZ=0
    g39: LineSegment StartX=-7.91979 StartY=9.10459 StartZ=0 EndX=-8.1464 EndY=11.6947 EndZ=0
    g40: LineSegment StartX=-8.1464 StartY=11.6947 StartZ=0 EndX=-8.26842 EndY=13.0894 EndZ=0
    g41: LineSegment StartX=0 StartY=13.8128 StartZ=0 EndX=0.348623 EndY=9.82798 EndZ=0
    g42: LineSegment StartX=7.32199 StartY=10.4381 StartZ=0 EndX=7.09538 EndY=13.0282 EndZ=0
    g43: LineSegment StartX=8.39043 StartY=13.1415 StartZ=0 EndX=8.26842 EndY=14.5362 EndZ=0
    g44: LineSegment StartX=-6.85134 StartY=11.808 StartZ=0 EndX=-6.62474 EndY=9.21789 EndZ=0
    g45: LineSegment StartX=14.2224 StartY=16.0299 StartZ=0 EndX=20.8002 EndY=18.4241 EndZ=0
    g46: LineSegment StartX=20.8002 StartY=18.4241 StartZ=0 EndX=27.3781 EndY=20.8182 EndZ=0
    g47: LineSegment StartX=27.3781 StartY=20.8182 StartZ=0 EndX=27.8569 EndY=19.5026 EndZ=0
    g48: LineSegment StartX=27.8569 StartY=19.5026 StartZ=0 EndX=29.0785 EndY=19.9473 EndZ=0
    g49: LineSegment StartX=29.0785 StartY=19.9473 StartZ=0 EndX=29.9678 EndY=17.5041 EndZ=0
    g50: LineSegment StartX=29.9678 StartY=17.5041 StartZ=0 EndX=22.1683 EndY=14.6653 EndZ=0
    g51: LineSegment StartX=22.1683 StartY=14.6653 StartZ=0 EndX=14.3689 EndY=11.8265 EndZ=0
    g52: LineSegment StartX=14.3689 StartY=11.8265 StartZ=0 EndX=13.4796 EndY=14.2697 EndZ=0
    g53: LineSegment StartX=13.4796 StartY=14.2697 StartZ=0 EndX=14.7012 EndY=14.7144 EndZ=0
    g54: LineSegment StartX=14.7012 StartY=14.7144 StartZ=0 EndX=14.2224 EndY=16.0299 EndZ=0
    g55: LineSegment StartX=20.8002 StartY=18.4241 StartZ=0 EndX=22.1683 EndY=14.6653 EndZ=0
    g56: LineSegment StartX=29.0785 StartY=19.9473 StartZ=0 EndX=28.5997 EndY=21.2628 EndZ=0
    g57: LineSegment StartX=27.8569 StartY=19.5026 StartZ=0 EndX=28.7462 EndY=17.0594 EndZ=0
    g58: LineSegment StartX=14.7012 StartY=14.7144 StartZ=0 EndX=15.5905 EndY=12.2711 EndZ=0
    g59: LineSegment StartX=13.4796 StartY=14.2697 StartZ=0 EndX=13.0008 EndY=15.5853 EndZ=0
    g60: LineSegment StartX=33.7023 StartY=22.3542 StartZ=0 EndX=34.7672 EndY=23.0999 EndZ=0
    g61: LineSegment StartX=34.7672 StartY=23.0999 StartZ=0 EndX=33.9642 EndY=24.2467 EndZ=0
    g62: LineSegment StartX=33.9642 StartY=24.2467 StartZ=0 EndX=39.6982 EndY=28.2617 EndZ=0
    g63: LineSegment StartX=39.6982 StartY=28.2617 StartZ=0 EndX=45.4323 EndY=32.2768 EndZ=0
    g64: LineSegment StartX=45.4323 StartY=32.2768 StartZ=0 EndX=46.2353 EndY=31.13 EndZ=0
    g65: LineSegment StartX=46.2353 StartY=31.13 StartZ=0 EndX=47.3002 EndY=31.8756 EndZ=0
    g66: LineSegment StartX=47.3002 StartY=31.8756 StartZ=0 EndX=48.7915 EndY=29.7458 EndZ=0
    g67: LineSegment StartX=48.7915 StartY=29.7458 StartZ=0 EndX=41.9925 EndY=24.9851 EndZ=0
    g68: LineSegment StartX=41.9925 StartY=24.9851 StartZ=0 EndX=35.1936 EndY=20.2244 EndZ=0
    g69: LineSegment StartX=35.1936 StartY=20.2244 StartZ=0 EndX=33.7023 EndY=22.3542 EndZ=0
    g70: LineSegment StartX=33.7023 StartY=22.3542 StartZ=0 EndX=32.8993 EndY=23.5011 EndZ=0
    g71: LineSegment StartX=46.4972 StartY=33.0224 StartZ=0 EndX=47.3002 EndY=31.8756 EndZ=0
    g72: LineSegment StartX=39.6982 StartY=28.2617 StartZ=0 EndX=41.9925 EndY=24.9851 EndZ=0
    g73: LineSegment StartX=36.2585 StartY=20.9701 StartZ=0 EndX=34.7672 EndY=23.0999 EndZ=0
    g74: LineSegment StartX=46.2353 StartY=31.13 StartZ=0 EndX=47.7266 EndY=29.0002 EndZ=0
  constraints (215):
    c: PointOnObject(g0,g-4)
    c: Coincident(g0,g-4)
    c: Coincident(g0,g1)
    c: PointOnObject(g1,g-3)
    c: Coincident(g1,g2)
    c: Coincident(g2,g3)
    c: Coincident(g3,g4)
    c: PointOnObject(g4,g-5)
    c: PointOnObject(g5,g-5)
    c: Coincident(g5,g6)
    c: Coincident(g6,g7)
    c: Coincident(g7,g0)
    c: Perpendicular(g-5,g5)
    c: Perpendicular(g-5,g4)
    c: Coincident(g8,g2)
    c: Coincident(g9,g6)
    c: Coincident(g10,g5)
    c: PointOnObject(g10,g-4)
    c: Coincident(g11,g3)
    c: PointOnObject(g11,g-3)
    c: Angle(g4,g11) = 3.14159
    c: Angle(g8,g2) = 3.14159
    c: Angle(g9,g7) = 3.14159
    c: Angle(g5,g10) = 3.14159
    c: Perpendicular(g-3,g2)
    c: Perpendicular(g-4,g7)
    c: Equal(g11,g2)
    c: Equal(g2,g7)
    c: Equal(g7,g10)
    c: Distance(g2) = 1.4
    c: Distance(g0,g1) = 14
    c: Equal(g0,g1)
    c: Coincident(g5,g12)
    c: PointOnObject(g12,g-5)
    c: Coincident(g12,g13)
    c: Coincident(g13,g4)
    c: Coincident(g14,g0)
    c: Coincident(g14,g12)
    c: Perpendicular(g-5,g14)
    c: Equal(g12,g13)
    c: Distance(g4,g5) = 16.6
    c: PointOnObject(g8,g-5)
    c: PointOnObject(g9,g-5)
    c: PointOnObject(g15,g-8)
    c: Coincident(g15,g16)
    c: Coincident(g16,g17)
    c: PointOnObject(g17,g-6)
    c: Coincident(g17,g18)
    c: Coincident(g18,g-7)
    c: Coincident(g18,g19)
    c: PointOnObject(g19,g-7)
    c: Coincident(g19,g20)
    c: Coincident(g20,g21)
    c: Coincident(g21,g22)
    c: PointOnObject(g22,g-8)
    c: Coincident(g22,g23)
    c: PointOnObject(g23,g-8)
    c: Coincident(g23,g24)
    c: Coincident(g15,g24)
    c: Coincident(g25,g15)
    c: PointOnObject(g25,g-6)
    c: Coincident(g26,g18)
    c: Coincident(g26,g23)
    c: Coincident(g27,g21)
    c: PointOnObject(g27,g-7)
    c: Coincident(g28,g20)
    c: PointOnObject(g28,g23)
    c: PointOnObject(g29,g24)
    c: Coincident(g29,g16)
    c: Angle(g25,g15) = 3.14159
    c: Angle(g17,g29) = 3.14159
    c: Angle(g20,g28) = 3.14159
    c: Angle(g22,g27) = 3.14159
    c: Perpendicular(g-7,g20)
    c: Perpendicular(g-8,g22)
    c: Perpendicular(g-8,g15)
    c: Perpendicular(g17,g-6)
    c: Perpendicular(g-8,g26)
    c: Equal(g23,g24)
    c: Equal(g18,g19)
    c: Equal(g27,g20)
    c: Equal(g20,g17)
    c: Equal(g17,g25)
    c: Distance(g20) = 1.4
    c: Distance(g19,g17) = 14
    c: Distance(g22,g15) = 16.6
    c: Coincident(g30,g31)
    c: PointOnObject(g31,g-9)
    c: Coincident(g31,g32)
    c: Coincident(g32,g-10)
    c: Coincident(g32,g33)
    c: PointOnObject(g33,g-10)
    c: Coincident(g33,g34)
    c: Coincident(g34,g35)
    c: Coincident(g35,g36)
    c: PointOnObject(g36,g-11)
    c: Coincident(g36,g37)
    c: PointOnObject(g37,g-11)
    c: Coincident(g37,g38)
    c: PointOnObject(g38,g-11)
    c: Coincident(g38,g39)
    c: Coincident(g39,g30)
    c: Coincident(g40,g30)
    c: PointOnObject(g40,g-9)
    c: Coincident(g41,g32)
    c: Coincident(g41,g37)
    c: PointOnObject(g42,g37)
    c: Coincident(g42,g34)
    c: Coincident(g43,g35)
    c: PointOnObject(g43,g-10)
    c: Angle(g36,g43) = 3.14159
    c: Angle(g42,g34) = 3.14159
    c: Angle(g39,g40) = 3.14159
    c: Coincident(g44,g30)
    c: PointOnObject(g44,g38)
    c: Angle(g31,g44) = 3.14159
    c: Equal(g40,g31)
    c: Equal(g31,g34)
    c: Equal(g34,g43)
    c: Perpendicular(g-10,g43)
    c: Perpendicular(g-10,g34)
    c: Perpendicular(g-9,g31)
    c: Perpendicular(g-9,g40)
    c: Perpendicular(g-11,g41)
    c: Distance(g33,g31) = 14
    c: Distance(g38,g36) = 16.6
    c: Distance(g34) = 1.4
    c: Equal(g33,g32)
    c: Equal(g38,g37)
    c: PointOnObject(g45,g-13)
    c: Coincident(g45,g-14)
    c: Coincident(g45,g46)
    c: PointOnObject(g46,g-14)
    c: Coincident(g46,g47)
    c: Coincident(g47,g48)
    c: Coincident(g48,g49)
    c: PointOnObject(g49,g-12)
    c: Coincident(g49,g50)
    c: PointOnObject(g50,g-12)
    c: Coincident(g50,g51)
    c: PointOnObject(g51,g-12)
    c: Coincident(g51,g52)
    c: Coincident(g52,g53)
    c: Coincident(g53,g54)
    c: Coincident(g54,g45)
    c: Coincident(g55,g45)
    c: Coincident(g55,g50)
    c: Coincident(g56,g48)
    c: PointOnObject(g56,g-14)
    c: Coincident(g57,g47)
    c: PointOnObject(g57,g50)
    c: Coincident(g58,g53)
    c: PointOnObject(g58,g51)
    c: PointOnObject(g59,g-13)
    c: Coincident(g59,g52)
    c: Angle(g52,g59) = 3.14159
    c: Angle(g58,g54) = 3.14159
    c: Angle(g47,g57) = 3.14159
    c: Angle(g56,g49) = 3.14159
    c: Distance(g46,g45) = 14
    c: Distance(g51,g49) = 16.6
    c: Distance(g47) = 1.4
    c: Equal(g56,g47)
    c: Equal(g47,g54)
    c: Equal(g54,g59)
    c: Equal(g45,g46)
    c: Equal(g51,g50)
    c: Perpendicular(g-12,g55)
    c: Perpendicular(g-12,g52)
    c: Perpendicular(g-13,g54)
    c: Perpendicular(g-14,g47)
    c: Perpendicular(g49,g-12)
    c: Coincident(g60,g61)
    c: PointOnObject(g61,g-15)
    c: Coincident(g61,g62)
    c: Coincident(g62,g-17)
    c: Coincident(g62,g63)
    c: PointOnObject(g63,g-17)
    c: Coincident(g63,g64)
    c: Coincident(g64,g65)
    c: Coincident(g65,g66)
    c: PointOnObject(g66,g-16)
    c: Coincident(g66,g67)
    c: PointOnObject(g67,g-16)
    c: Coincident(g67,g68)
    c: PointOnObject(g68,g-16)
    c: Coincident(g68,g69)
    c: Coincident(g69,g60)
    c: Coincident(g70,g60)
    c: PointOnObject(g70,g-15)
    c: PointOnObject(g71,g-17)
    c: Coincident(g71,g65)
    c: Coincident(g72,g62)
    c: Coincident(g72,g67)
    c: PointOnObject(g73,g68)
    c: Coincident(g73,g60)
    c: PointOnObject(g74,g67)
    c: Coincident(g64,g74)
    c: Angle(g66,g71) = 3.14159
    c: Angle(g74,g64) = 3.14159
    c: Angle(g61,g73) = 3.14159
    c: Angle(g70,g69) = 3.14159
    c: Perpendicular(g-16,g69)
    c: Perpendicular(g-15,g61)
    c: Perpendicular(g-17,g64)
    c: Perpendicular(g-16,g66)
    c: Equal(g64,g71)
    c: Equal(g71,g61)
    c: Equal(g61,g70)
    c: Equal(g62,g63)
    c: Equal(g67,g68)
    c: Perpendicular(g-15,g72)
    c: Distance(g64) = 1.4
    c: Distance(g63,g61) = 14
    c: Distance(g66,g68) = 16.6
FEATURE [PartDesign::Pocket] Pocket006  label="MMX Sockets"
  BaseFeature = -> Pad012
  Direction = (-1,2e-16,-3e-16)
  Length = 14
  Length2 = 100
  Midplane = true
  Placement = pos=(0,0,0) rot=(0.57735,0.57735,0.57735;2.0944rad)
  Profile = -> Sketch021
  Type = 0
FEATURE [Sketcher::SketchObject] Sketch022
  ExternalGeometry = -> [Sketch021]
  FullyConstrained = true
  MapMode = 5
  Placement = pos=(0,0,0) rot=(0.57735,0.57735,0.57735;2.0944rad)
  Support = -> [YZ_Plane003]
  sketch-geometry (55):
    g0: LineSegment StartX=-48.4555 StartY=23.0195 StartZ=0 EndX=-35.7672 EndY=17.1028 EndZ=0
    g1: LineSegment StartX=-35.7672 StartY=17.1028 StartZ=0 EndX=-35.8517 EndY=16.9215 EndZ=0
    g2: LineSegment StartX=-35.8517 StartY=16.9215 StartZ=0 EndX=-34.6735 EndY=16.3721 EndZ=0
    g3: LineSegment StartX=-34.6735 StartY=16.3721 StartZ=0 EndX=-35.0116 EndY=15.6471 EndZ=0
    g4: LineSegment StartX=-35.0116 StartY=15.6471 StartZ=0 EndX=-50.0563 EndY=22.6626 EndZ=0
    g5: LineSegment StartX=-50.0563 StartY=22.6626 StartZ=0 EndX=-49.7182 EndY=23.3876 EndZ=0
    g6: LineSegment StartX=-49.7182 StartY=23.3876 StartZ=0 EndX=-48.54 EndY=22.8382 EndZ=0
    g7: LineSegment StartX=-48.54 StartY=22.8382 StartZ=0 EndX=-48.4555 EndY=23.0195 EndZ=0
    g8: LineSegment StartX=-41.6042 StartY=21.1487 StartZ=0 EndX=-42.1113 EndY=20.0611 EndZ=0
    g9: LineSegment StartX=-42.1113 StartY=20.0611 StartZ=0 EndX=-42.5339 EndY=19.1548 EndZ=0
    g10: LineSegment StartX=-42.5339 StartY=19.1548 StartZ=0 EndX=-43.2946 EndY=17.5235 EndZ=0
    g11: LineSegment StartX=-28.387 StartY=14.7758 StartZ=0 EndX=-14.5997 EndY=12.3448 EndZ=0
    g12: LineSegment StartX=-14.5997 StartY=12.3448 StartZ=0 EndX=-14.6344 EndY=12.1478 EndZ=0
    g13: LineSegment StartX=-14.6344 StartY=12.1478 StartZ=0 EndX=-13.3542 EndY=11.9221 EndZ=0
    g14: LineSegment StartX=-13.3542 StartY=11.9221 StartZ=0 EndX=-13.4931 EndY=11.1342 EndZ=0
    g15: LineSegment StartX=-13.4931 StartY=11.1342 StartZ=0 EndX=-29.8409 EndY=14.0168 EndZ=0
    g16: LineSegment StartX=-29.8409 StartY=14.0168 StartZ=0 EndX=-29.702 EndY=14.8046 EndZ=0
    g17: LineSegment StartX=-29.702 StartY=14.8046 StartZ=0 EndX=-28.4217 EndY=14.5789 EndZ=0
    g18: LineSegment StartX=-28.4217 StartY=14.5789 StartZ=0 EndX=-28.387 EndY=14.7758 EndZ=0
    g19: LineSegment StartX=-21.285 StartY=14.7421 StartZ=0 EndX=-21.4934 EndY=13.5603 EndZ=0
    g20: LineSegment StartX=-21.667 StartY=12.5755 StartZ=0 EndX=-21.4934 EndY=13.5603 EndZ=0
    g21: LineSegment StartX=-21.667 StartY=12.5755 StartZ=0 EndX=-21.9796 EndY=10.8028 EndZ=0
    g22: LineSegment StartX=-6.86878 StartY=12.0072 StartZ=0 EndX=7.07795 EndY=13.2274 EndZ=0
    g23: LineSegment StartX=7.07795 StartY=13.2274 StartZ=0 EndX=7.09538 EndY=13.0282 EndZ=0
    g24: LineSegment StartX=7.09538 StartY=13.0282 StartZ=0 EndX=8.39043 EndY=13.1415 EndZ=0
    g25: LineSegment StartX=8.39043 StartY=13.1415 StartZ=0 EndX=8.46016 EndY=12.3445 EndZ=0
    g26: LineSegment StartX=8.46016 StartY=12.3445 StartZ=0 EndX=-8.07667 EndY=10.8977 EndZ=0
    g27: LineSegment StartX=-8.07667 StartY=10.8977 StartZ=0 EndX=-8.1464 EndY=11.6947 EndZ=0
    g28: LineSegment StartX=-8.1464 StartY=11.6947 StartZ=0 EndX=-6.85134 EndY=11.808 EndZ=0
    g29: LineSegment StartX=-6.85134 StartY=11.808 StartZ=0 EndX=-6.86878 EndY=12.0072 EndZ=0
    g30: LineSegment StartX=5.8389e-12 StartY=13.8128 StartZ=0 EndX=0.104587 EndY=12.6173 EndZ=0
    g31: LineSegment StartX=0.104587 StartY=12.6173 StartZ=0 EndX=0.191743 EndY=11.6211 EndZ=0
    g32: LineSegment StartX=0.191743 StartY=11.6211 StartZ=0 EndX=0.348623 EndY=9.82798 EndZ=0
    g33: LineSegment StartX=14.6328 StartY=14.9023 StartZ=0 EndX=27.7885 EndY=19.6906 EndZ=0
    g34: LineSegment StartX=27.7885 StartY=19.6906 StartZ=0 EndX=27.8569 EndY=19.5026 EndZ=0
    g35: LineSegment StartX=27.8569 StartY=19.5026 StartZ=0 EndX=29.0785 EndY=19.9473 EndZ=0
    g36: LineSegment StartX=29.0785 StartY=19.9473 StartZ=0 EndX=29.3521 EndY=19.1955 EndZ=0
    g37: LineSegment StartX=29.3521 StartY=19.1955 StartZ=0 EndX=13.7532 EndY=13.518 EndZ=0
    g38: LineSegment StartX=13.7532 StartY=13.518 StartZ=0 EndX=13.4796 EndY=14.2697 EndZ=0
    g39: LineSegment StartX=13.4796 StartY=14.2697 StartZ=0 EndX=14.7012 EndY=14.7144 EndZ=0
    g40: LineSegment StartX=14.7012 StartY=14.7144 StartZ=0 EndX=14.6328 EndY=14.9023 EndZ=0
    g41: LineSegment StartX=20.8002 StartY=18.4241 StartZ=0 EndX=21.2107 EndY=17.2964 EndZ=0
    g42: LineSegment StartX=21.2107 StartY=17.2964 StartZ=0 EndX=21.5527 EndY=16.3567 EndZ=0
    g43: LineSegment StartX=21.5527 StartY=16.3567 StartZ=0 EndX=22.1683 EndY=14.6653 EndZ=0
    g44: LineSegment StartX=34.6525 StartY=23.2637 StartZ=0 EndX=46.1206 EndY=31.2938 EndZ=0
    g45: LineSegment StartX=46.1206 StartY=31.2938 StartZ=0 EndX=46.2353 EndY=31.13 EndZ=0
    g46: LineSegment StartX=46.2353 StartY=31.13 StartZ=0 EndX=47.3002 EndY=31.8756 EndZ=0
    g47: LineSegment StartX=47.3002 StartY=31.8756 StartZ=0 EndX=47.7591 EndY=31.2203 EndZ=0
    g48: LineSegment StartX=47.7591 StartY=31.2203 StartZ=0 EndX=34.1611 EndY=21.6989 EndZ=0
    g49: LineSegment StartX=34.1611 StartY=21.6989 StartZ=0 EndX=33.7023 EndY=22.3542 EndZ=0
    g50: LineSegment StartX=33.7023 StartY=22.3542 StartZ=0 EndX=34.7672 EndY=23.0999 EndZ=0
    g51: LineSegment StartX=34.7672 StartY=23.0999 StartZ=0 EndX=34.6525 EndY=23.2637 EndZ=0
    g52: LineSegment StartX=39.6982 StartY=28.2617 StartZ=0 EndX=40.3865 EndY=27.2788 EndZ=0
    g53: LineSegment StartX=40.3865 StartY=27.2788 StartZ=0 EndX=40.9601 EndY=26.4596 EndZ=0
    g54: LineSegment StartX=40.9601 StartY=26.4596 StartZ=0 EndX=41.9925 EndY=24.9851 EndZ=0
  constraints (140):
    c: PointOnObject(g0,g-5)
    c: Coincident(g0,g1)
    c: Coincident(g1,g-5)
    c: Coincident(g1,g2)
    c: Coincident(g2,g-6)
    c: Coincident(g2,g3)
    c: PointOnObject(g3,g-6)
    c: Coincident(g3,g4)
    c: PointOnObject(g4,g-4)
    c: Coincident(g4,g5)
    c: Coincident(g5,g-4)
    c: Coincident(g5,g6)
    c: Coincident(g6,g-3)
    c: Coincident(g6,g7)
    c: Coincident(g7,g0)
    c: PointOnObject(g0,g-3)
    c: Coincident(g8,g-23)
    c: PointOnObject(g8,g0)
    c: Coincident(g8,g9)
    c: PointOnObject(g9,g4)
    c: Coincident(g9,g10)
    c: Coincident(g10,g-24)
    c: Angle(g9,g8) = 3.14159
    c: Distance(g8) = 1.2
    c: Distance(g9) = 1
    c: Perpendicular(g0,g8)
    c: Perpendicular(g9,g4)
    c: Angle(g9,g10) = 3.14159
    c: PointOnObject(g11,g-7)
    c: PointOnObject(g11,g-9)
    c: Coincident(g11,g12)
    c: Coincident(g12,g-9)
    c: Coincident(g12,g13)
    c: Coincident(g13,g14)
    c: PointOnObject(g14,g-10)
    c: Coincident(g14,g15)
    c: PointOnObject(g15,g-8)
    c: Coincident(g15,g16)
    c: Coincident(g16,g-8)
    c: Coincident(g16,g17)
    c: Coincident(g17,g-7)
    c: Coincident(g17,g18)
    c: Coincident(g18,g11)
    c: Coincident(g-10,g13)
    c: Coincident(g19,g-25)
    c: PointOnObject(g19,g11)
    c: PointOnObject(g20,g15)
    c: Coincident(g20,g19)
    c: Coincident(g21,g-26)
    c: Coincident(g21,g20)
    c: Angle(g21,g20) = 3.14159
    c: Angle(g19,g20) = 3.14159
    c: Distance(g19) = 1.2
    c: Distance(g20) = 1
    c: Perpendicular(g19,g11)
    c: Perpendicular(g21,g15)
    c: PointOnObject(g22,g-11)
    c: PointOnObject(g22,g-13)
    c: Coincident(g22,g23)
    c: Coincident(g23,g-13)
    c: Coincident(g23,g24)
    c: Coincident(g24,g-14)
    c: Coincident(g24,g25)
    c: PointOnObject(g25,g-14)
    c: Coincident(g25,g26)
    c: PointOnObject(g26,g-12)
    c: Coincident(g26,g27)
    c: Coincident(g27,g-12)
    c: Coincident(g27,g28)
    c: Coincident(g28,g-11)
    c: Coincident(g28,g29)
    c: Coincident(g29,g22)
    c: Coincident(g-28,g30)
    c: PointOnObject(g30,g22)
    c: Coincident(g30,g31)
    c: PointOnObject(g31,g26)
    c: Coincident(g31,g32)
    c: Angle(g32,g31) = 3.14159
    c: Angle(g31,g30) = 3.14159
    c: Perpendicular(g22,g31)
    c: Perpendicular(g26,g31)
    c: Distance(g30) = 1.2
    c: Distance(g31) = 1
    c: Coincident(g32,g-27)
    c: PointOnObject(g33,g-16)
    c: PointOnObject(g33,g-17)
    c: Coincident(g33,g34)
    c: Coincident(g34,g-17)
    c: Coincident(g34,g35)
    c: Coincident(g35,g-18)
    c: Coincident(g35,g36)
    c: PointOnObject(g36,g-18)
    c: Coincident(g36,g37)
    c: PointOnObject(g37,g-15)
    c: Coincident(g37,g38)
    c: Coincident(g38,g-15)
    c: Coincident(g38,g39)
    c: Coincident(g39,g-16)
    c: Coincident(g39,g40)
    c: Coincident(g40,g33)
    c: Coincident(g41,g-29)
    c: PointOnObject(g41,g33)
    c: Coincident(g41,g42)
    c: PointOnObject(g42,g37)
    c: Coincident(g42,g43)
    c: Coincident(g43,g-30)
    c: Angle(g42,g43) = 3.14159
    c: Angle(g41,g42) = 3.14159
    c: Distance(g41) = 1.2
    c: Distance(g42) = 1
    c: Perpendicular(g41,g33)
    c: Perpendicular(g42,g37)
    c: PointOnObject(g44,g-20)
    c: PointOnObject(g44,g-21)
    c: Coincident(g44,g45)
    c: Coincident(g45,g-21)
    c: Coincident(g45,g46)
    c: Coincident(g46,g-22)
    c: Coincident(g46,g47)
    c: PointOnObject(g47,g-22)
    c: Coincident(g47,g48)
    c: PointOnObject(g48,g-19)
    c: Coincident(g48,g49)
    c: Coincident(g49,g-19)
    c: Coincident(g49,g50)
    c: Coincident(g50,g-20)
    c: Coincident(g50,g51)
    c: Coincident(g51,g44)
    c: Coincident(g52,g-31)
    c: PointOnObject(g52,g44)
    c: Coincident(g52,g53)
    c: PointOnObject(g53,g48)
    c: Coincident(g53,g54)
    c: Coincident(g54,g-32)
    c: Angle(g53,g54) = 3.14159
    c: Angle(g53,g52) = 3.14159
    c: Distance(g52) = 1.2
    c: Distance(g53) = 1
    c: Perpendicular(g52,g44)
    c: Perpendicular(g48,g53)
FEATURE [PartDesign::Pocket] Pocket007  label="MChoc Sockets"
  BaseFeature = -> Pocket006
  Direction = (-1,2e-16,-3e-16)
  Length = 14.6
  Length2 = 100
  Midplane = true
  Placement = pos=(0,0,0) rot=(0.57735,0.57735,0.57735;2.0944rad)
  Profile = -> Sketch022
  Type = 0
FEATURE [Sketcher::SketchObject] Sketch023
  ExternalGeometry = -> [Sketch020]
  FullyConstrained = true
  MapMode = 5
  Placement = pos=(0,0,0) rot=(0.57735,0.57735,0.57735;2.0944rad)
  Support = -> [YZ_Plane003]
  expr: Constraints[39] = <<Spreadsheet>>.Wiring
  sketch-geometry (16):
    g0: LineSegment StartX=-11.9293 StartY=13.0924 StartZ=0 EndX=-9.46385 EndY=12.9848 EndZ=0
    g1: LineSegment StartX=-9.46385 StartY=12.9848 StartZ=0 EndX=-9.11523 EndY=9 EndZ=0
    g2: LineSegment StartX=-9.11523 StartY=9 StartZ=0 EndX=-8.59229 EndY=3.02283 EndZ=0
    g3: LineSegment StartX=-8.59229 StartY=3.02283 StartZ=0 EndX=-8.59229 EndY=0 EndZ=0
    g4: LineSegment StartX=-8.59229 StartY=0 StartZ=0 EndX=-13.6658 EndY=0 EndZ=0
    g5: LineSegment StartX=-13.6658 StartY=0 StartZ=0 EndX=-13.6658 EndY=3.24435 EndZ=0
    g6: LineSegment StartX=-13.6658 StartY=3.24435 StartZ=0 EndX=-12.6239 EndY=9.15319 EndZ=0
    g7: LineSegment StartX=-12.6239 StartY=9.15319 StartZ=0 EndX=-11.9293 EndY=13.0924 EndZ=0
    g8: LineSegment StartX=9.81247 StartY=10.656 StartZ=0 EndX=9.46385 EndY=14.6407 EndZ=0
    g9: LineSegment StartX=9.46385 StartY=14.6407 StartZ=0 EndX=11.8732 EndY=15.1749 EndZ=0
    g10: LineSegment StartX=11.8732 StartY=15.1749 StartZ=0 EndX=13.2412 EndY=11.4161 EndZ=0
    g11: LineSegment StartX=13.2412 StartY=11.4161 StartZ=0 EndX=15.2934 EndY=5.77794 EndZ=0
    g12: LineSegment StartX=15.2934 StartY=5.77794 StartZ=0 EndX=15.2934 EndY=0 EndZ=0
    g13: LineSegment StartX=15.2934 StartY=0 StartZ=0 EndX=10.3354 EndY=0 EndZ=0
    g14: LineSegment StartX=10.3354 StartY=0 StartZ=0 EndX=10.3354 EndY=4.67879 EndZ=0
    g15: LineSegment StartX=10.3354 StartY=4.67879 StartZ=0 EndX=9.81247 EndY=10.656 EndZ=0
  constraints (40):
    c: Coincident(g-3,g0)
    c: Coincident(g0,g-3)
    c: Coincident(g0,g1)
    c: Coincident(g1,g-4)
    c: Coincident(g1,g2)
    c: Coincident(g2,g3)
    c: PointOnObject(g3,g-1)
    c: Vertical(g3)
    c: Coincident(g3,g4)
    c: PointOnObject(g4,g-1)
    c: Coincident(g4,g5)
    c: Vertical(g5)
    c: Coincident(g5,g6)
    c: Coincident(g6,g-4)
    c: Coincident(g6,g7)
    c: Coincident(g7,g0)
    c: Angle(g1,g2) = 3.14159
    c: Angle(g6,g7) = 3.14159
    c: Coincident(g-6,g8)
    c: Coincident(g8,g-5)
    c: Coincident(g8,g9)
    c: Coincident(g9,g-5)
    c: Coincident(g9,g10)
    c: Coincident(g10,g-6)
    c: Coincident(g10,g11)
    c: Coincident(g11,g12)
    c: PointOnObject(g12,g-1)
    c: Coincident(g12,g13)
    c: PointOnObject(g13,g-1)
    c: Coincident(g13,g14)
    c: Vertical(g14)
    c: Coincident(g14,g15)
    c: Coincident(g15,g8)
    c: Vertical(g12)
    c: Angle(g10,g11) = 3.14159
    c: Angle(g8,g15) = 3.14159
    c: Equal(g11,g15)
    c: Equal(g15,g2)
    c: Equal(g2,g6)
    c: Distance(g6) = 6
FEATURE [PartDesign::Pad] Pad013  label="MInner Legs"
  BaseFeature = -> Pocket007
  Direction = (1,-2e-16,3e-16)
  Length = 4.1
  Length2 = 9.5
  Placement = pos=(0,0,0) rot=(0.57735,0.57735,0.57735;2.0944rad)
  Profile = -> Sketch023
  ReferenceAxis = -> Sketch023 [N_Axis]
  Type = 4
  expr: Length = <<Spreadsheet>>.ScrewD / 2 + 2mm
FEATURE [Sketcher::SketchObject] Sketch024
  ExternalGeometry = -> [Sketch020]
  FullyConstrained = true
  MapMode = 5
  Placement = pos=(0,0,0) rot=(0.57735,0.57735,0.57735;2.0944rad)
  Support = -> [YZ_Plane003]
  expr: Constraints[27] = <<Spreadsheet>>.Wiring
  expr: Constraints[36] = <<Spreadsheet>>.ArchLength - 5mm
  expr: Constraints[37] = <<Spreadsheet>>.ArchLength
  expr: Constraints[38] = <<Spreadsheet>>.ArchLength - 5mm
  expr: Constraints[39] = <<Spreadsheet>>.ArchLength
  expr: Constraints[40] = <<Spreadsheet>>.ArchLength - 10mm
  expr: Constraints[41] = <<Spreadsheet>>.ArchLength - 10mm
  sketch-geometry (36):
    g0: LineSegment StartX=-35 StartY=0 StartZ=0 EndX=-32.3771 EndY=6.54366 EndZ=0
    g1: LineSegment StartX=-32.3771 StartY=6.54366 StartZ=0 EndX=-31.3353 EndY=12.4525 EndZ=0
    g2: LineSegment StartX=-31.3353 StartY=12.4525 StartZ=0 EndX=-30.6407 EndY=16.3917 EndZ=0
    g3: LineSegment StartX=-30.6407 StartY=16.3917 StartZ=0 EndX=-32.9942 EndY=17.1338 EndZ=0
    g4: LineSegment StartX=-32.9942 StartY=17.1338 StartZ=0 EndX=-34.6847 EndY=13.5086 EndZ=0
    g5: LineSegment StartX=-34.6847 StartY=13.5086 StartZ=0 EndX=-37.2204 EndY=8.07075 EndZ=0
    g6: LineSegment StartX=45 StartY=3 StartZ=0 EndX=45 EndY=0 EndZ=0
    g7: LineSegment StartX=45 StartY=0 StartZ=0 EndX=35 EndY=0 EndZ=0
    g8: LineSegment StartX=35 StartY=0 StartZ=0 EndX=33.1475 EndY=12.2763 EndZ=0
    g9: LineSegment StartX=33.1475 StartY=12.2763 StartZ=0 EndX=31.0954 EndY=17.9145 EndZ=0
    g10: LineSegment StartX=31.0954 StartY=17.9145 StartZ=0 EndX=29.7273 EndY=21.6733 EndZ=0
    g11: LineSegment StartX=29.7273 StartY=21.6733 StartZ=0 EndX=31.9163 EndY=22.8128 EndZ=0
    g12: LineSegment StartX=31.9163 StartY=22.8128 StartZ=0 EndX=34.2106 EndY=19.5362 EndZ=0
    g13: LineSegment StartX=34.2106 StartY=19.5362 StartZ=0 EndX=37.6521 EndY=14.6212 EndZ=0
    g14: LineSegment StartX=-35 StartY=0 StartZ=0 EndX=-45 EndY=0 EndZ=0
    g15: LineSegment StartX=-45 StartY=0 StartZ=0 EndX=-45 EndY=3 EndZ=0
    g16: LineSegment StartX=-45 StartY=3 StartZ=0 EndX=-40 EndY=3 EndZ=0
    g17: LineSegment StartX=40 StartY=3 StartZ=0 EndX=45 EndY=3 EndZ=0
    g18: LineSegment StartX=37.6521 StartY=14.6212 StartZ=0 EndX=42.2621 EndY=8.03739 EndZ=0
    g19: LineSegment StartX=42.2621 StartY=8.03739 StartZ=0 EndX=42.2621 EndY=0 EndZ=0
    g20: LineSegment StartX=-37.2204 StartY=8.07075 StartZ=0 EndX=-39.0097 EndY=4.23371 EndZ=0
    g21: LineSegment StartX=-39.0097 StartY=4.23371 StartZ=0 EndX=-39.0097 EndY=0 EndZ=0
    g22-g25: Circle x4 (B-spline internal-alignment scaffolding for g26; pole/knot coordinates omitted)
    g26: BSplineCurve PolesCount=4 KnotsCount=2 Degree=3 IsPeriodic=0
    g27: GeomPoint X=-37.2204 Y=8.07075 Z=0
    g28: GeomPoint X=-45 Y=3 Z=0
    g29-g32: Circle x4 (B-spline internal-alignment scaffolding for g33; pole/knot coordinates omitted)
    g33: BSplineCurve PolesCount=4 KnotsCount=2 Degree=3 IsPeriodic=0
    g34: GeomPoint X=37.6521 Y=14.6212 Z=0
    g35: GeomPoint X=45 Y=3 Z=0
  constraints (82):
    c: PointOnObject(g0,g-1)
    c: Coincident(g0,g1)
    c: Coincident(g1,g-5)
    c: Coincident(g1,g2)
    c: Coincident(g2,g-6)
    c: Coincident(g2,g3)
    c: Coincident(g3,g-6)
    c: Coincident(g3,g4)
    c: Coincident(g4,g-5)
    c: Coincident(g4,g5)
    c: PointOnObject(g6,g-1)
    c: Vertical(g6)
    c: Coincident(g6,g7)
    c: PointOnObject(g7,g-1)
    c: Coincident(g7,g8)
    c: Coincident(g8,g9)
    c: Coincident(g9,g-4)
    c: Coincident(g9,g10)
    c: Coincident(g10,g-3)
    c: Coincident(g10,g11)
    c: Coincident(g11,g-3)
    c: Coincident(g11,g12)
    c: Coincident(g12,g-4)
    c: Coincident(g12,g13)
    c: Equal(g13,g9)
    c: Equal(g9,g1)
    c: Equal(g1,g5)
    c: Distance(g5) = 6
    c: Coincident(g14,g0)
    c: PointOnObject(g14,g-1)
    c: Coincident(g15,g14)
    c: Vertical(g15)
    c: Coincident(g16,g15)
    c: Horizontal(g16)
    c: Coincident(g17,g6)
    c: Horizontal(g17)
    c: DistanceX(g-7,g17) = 40
    c: DistanceX(g-7,g6) = 45
    c: DistanceX(g16,g-7) = 40
    c: DistanceX(g15,g-7) = 45
    c: DistanceX(g-7,g7) = 35
    c: DistanceX(g0,g-7) = 35
    c: Angle(g1,g2) = 3.14159
    c: Angle(g5,g4) = 3.14159
    c: Angle(g13,g12) = 3.14159
    c: Angle(g9,g10) = 3.14159
    c: Coincident(g13,g18)
    c: Coincident(g18,g19)
    c: PointOnObject(g19,g-1)
    c: Vertical(g19)
    c: Coincident(g5,g20)
    c: Coincident(g20,g21)
    c: PointOnObject(g21,g-1)
    c: Vertical(g21)
    c: Equal(g20,g21)
    c: Equal(g18,g19)
    c: Angle(g18,g13) = 3.14159
    c: DistanceY(g6,g6) = 3
    c: Equal(g15,g6)
    c: Angle(g5,g20) = 3.14159
    c: Coincident(g26,g5)
    c: Weight(g22) = 1
    c: Equal(g22,g23)
    c: Coincident(g23,g20)
    c: Equal(g22,g24)
    c: Coincident(g24,g16)
    c: Equal(g22,g25)
    c: Coincident(g26,g15)
    c: InternalAlignment(g22-g25 -> g26) x4
    c: InternalAlignment(g27,g26)
    c: InternalAlignment(g28,g26)
    c: Coincident(g33,g13)
    c: Weight(g29) = 1
    c: Equal(g29,g30)
    c: Coincident(g30,g18)
    c: Equal(g29,g31)
    c: Coincident(g31,g17)
    c: Equal(g29,g32)
    c: Coincident(g33,g6)
    c: InternalAlignment(g29-g32 -> g33) x4
    c: InternalAlignment(g34,g33)
    c: InternalAlignment(g35,g33)
FEATURE [PartDesign::Pad] Pad014  label="MOuterLegs"
  BaseFeature = -> Pad013
  Direction = (1,-2e-16,3e-16)
  Length = 9.5
  Length2 = 100
  Placement = pos=(0,0,0) rot=(0.57735,0.57735,0.57735;2.0944rad)
  Profile = -> Sketch024
  Reversed = true
  Type = 0
FEATURE [Sketcher::SketchObject] Sketch025
  ExternalGeometry = -> [Sketch024]
  FullyConstrained = true
  MapMode = 5
  Support = -> [XY_Plane003]
  expr: Constraints[21] = <<Spreadsheet>>.NutR
  expr: Constraints[22] = <<Spreadsheet>>.NutR
  expr: Constraints[28] = <<Spreadsheet>>.ScrewD
  expr: Constraints[54] = <<Spreadsheet>>.NutR
  expr: Constraints[55] = <<Spreadsheet>>.NutR
  expr: Constraints[57] = <<Spreadsheet>>.ScrewD
  sketch-geometry (22):
    g0: LineSegment StartX=1.33e-14 StartY=45 StartZ=0 EndX=-9.5 EndY=45 EndZ=0
    g1: LineSegment StartX=-9.5 StartY=45 StartZ=0 EndX=-9.5 EndY=55 EndZ=0
    g2: LineSegment StartX=-9.5 StartY=55 StartZ=0 EndX=4.5 EndY=55 EndZ=0
    g3: ArcOfCircle CenterX=4.5 CenterY=50 CenterZ=0 NormalX=0 NormalY=0 NormalZ=1 AngleXU=0 Radius=5 StartAngle=5.38688 EndAngle=7.85398
    g4: LineSegment StartX=9.5 StartY=50 StartZ=0 EndX=9.5 EndY=55 EndZ=0
    g5: LineSegment StartX=9.5 StartY=55 StartZ=0 EndX=0 EndY=50 EndZ=0
    g6: LineSegment StartX=0 StartY=50 StartZ=0 EndX=-9.5 EndY=55 EndZ=0
    g7: LineSegment StartX=1.33e-14 StartY=45 StartZ=0 EndX=9e-16 EndY=40 EndZ=0
    g8: LineSegment StartX=7.6225 StartY=46.0949 StartZ=0 EndX=9e-16 EndY=40 EndZ=0
    g9: Circle CenterX=0 CenterY=50 CenterZ=0 NormalX=0 NormalY=0 NormalZ=1 AngleXU=0 Radius=2.1
    g10: LineSegment StartX=0 StartY=50 StartZ=0 EndX=9.5 EndY=50 EndZ=0
    g11: LineSegment StartX=-9.8e-15 StartY=-45 StartZ=0 EndX=-9.5 EndY=-45 EndZ=0
    g12: LineSegment StartX=-9.5 StartY=-45 StartZ=0 EndX=-9.5 EndY=-55 EndZ=0
    g13: LineSegment StartX=-9.5 StartY=-55 StartZ=0 EndX=4.5 EndY=-55 EndZ=0
    g14: ArcOfCircle CenterX=4.5 CenterY=-50 CenterZ=0 NormalX=0 NormalY=0 NormalZ=1 AngleXU=0 Radius=5 StartAngle=4.71239 EndAngle=7.17949
    g15: LineSegment StartX=7.6225 StartY=-46.0949 StartZ=0 EndX=-9.8e-15 EndY=-40 EndZ=0
    g16: LineSegment StartX=-9.8e-15 StartY=-40 StartZ=0 EndX=-9.8e-15 EndY=-45 EndZ=0
    g17: LineSegment StartX=9.5 StartY=-50 StartZ=0 EndX=9.5 EndY=-55 EndZ=0
    g18: LineSegment StartX=9.5 StartY=-55 StartZ=0 EndX=0 EndY=-50 EndZ=0
    g19: LineSegment StartX=0 StartY=-50 StartZ=0 EndX=-9.5 EndY=-55 EndZ=0
    g20: LineSegment StartX=0 StartY=-50 StartZ=0 EndX=9.5 EndY=-50 EndZ=0
    g21: Circle CenterX=0 CenterY=-50 CenterZ=0 NormalX=0 NormalY=0 NormalZ=1 AngleXU=0 Radius=2.1
  constraints (58):
    c: Coincident(g0,g-3)
    c: Horizontal(g0)
    c: Coincident(g0,g1)
    c: Vertical(g1)
    c: Coincident(g1,g2)
    c: Tangent(g2,g3) = 1.5708
    c: Horizontal(g2)
    c: PointOnObject(g4,g3)
    c: Vertical(g4)
    c: Coincident(g4,g5)
    c: PointOnObject(g5,g-2)
    c: Coincident(g5,g6)
    c: Coincident(g6,g1)
    c: Coincident(g7,g0)
    c: PointOnObject(g7,g-2)
    c: Coincident(g8,g7)
    c: Tangent(g8,g3) = 1.5708
    c: Equal(g5,g6)
    c: Horizontal(g4,g2)
    c: DistanceX(g1,g4) = 19
    c: Coincident(g9,g5)
    c: DistanceY(g9,g1) = 5
    c: DistanceY(g0,g9) = 5
    c: DistanceY(g7,g7) = 5
    c: Coincident(g10,g9)
    c: Coincident(g10,g4)
    c: Horizontal(g10)
    c: PointOnObject(g3,g10)
    c: Diameter(g9) = 4.2
    c: Coincident(g11,g-4)
    c: Horizontal(g11)
    c: Coincident(g11,g12)
    c: Vertical(g12)
    c: Coincident(g12,g13)
    c: Horizontal(g13)
    c: Tangent(g13,g14) = -1.5708
    c: Tangent(g14,g15) = -1.5708
    c: Coincident(g15,g16)
    c: Coincident(g16,g11)
    c: Vertical(g16)
    c: DistanceY(g16,g16) = 5
    c: PointOnObject(g17,g14)
    c: Coincident(g17,g18)
    c: PointOnObject(g18,g-2)
    c: Coincident(g18,g19)
    c: Coincident(g19,g12)
    c: Equal(g19,g18)
    c: Vertical(g17)
    c: DistanceX(g12,g17) = 19
    c: Horizontal(g17,g13)
    c: Coincident(g20,g18)
    c: Coincident(g20,g17)
    c: Horizontal(g20)
    c: PointOnObject(g14,g20)
    c: DistanceY(g18,g11) = 5
    c: DistanceY(g12,g18) = 5
    c: Coincident(g21,g18)
    c: Diameter(g21) = 4.2
FEATURE [PartDesign::Pad] Pad015  label="Mfeet"
  BaseFeature = -> Pad014
  Direction = (0,0,1)
  Length = 3
  Length2 = 100
  Placement = pos=(0,0,0) rot=(0.57735,0.57735,0.57735;2.0944rad)
  Profile = -> Sketch025
  Type = 0
FEATURE [PartDesign::Body] Body003  label="MiddleArch"
  Group = -> [Sketch020,Pad012,Sketch021,Pocket006,Sketch022,Pocket007,Sketch023,Pad013,Sketch024,Pad014,Sketch025,Pad015]
  Origin = -> Origin003
  Placement = pos=(70,5,0) rot=(0,0,1;0rad)
  Tip = -> Pad015
